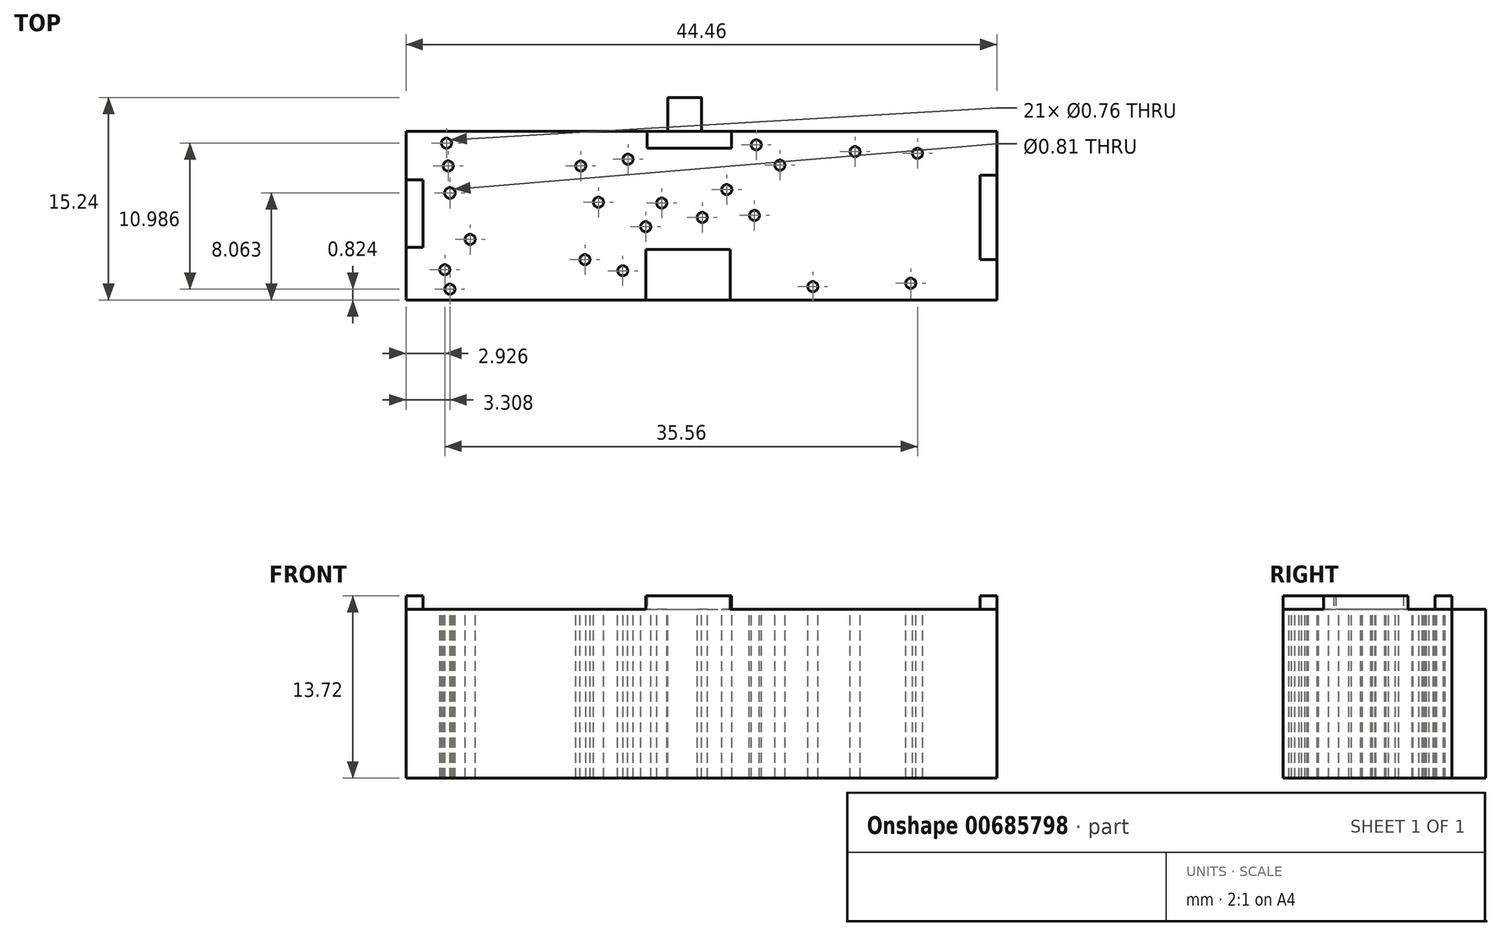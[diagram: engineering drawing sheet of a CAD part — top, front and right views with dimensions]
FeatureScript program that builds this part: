
annotation { "Feature Type Name" : "Feature", "Feature Type Description" : "" }
export const myFeature = defineFeature(function(context is Context, id is Id, definition is map)
    precondition{}
    {
        {
            var Q0;
            Q0=qCreatedBy(makeId("Top.planeOp"),FACE);
            var sketch = newSketch(context, id + "F0", { "sketchPlane" : qUnion([Q0])});
            skLineSegment(sketch, "E0", {"start": v(-5.35, -3.97) * mm, "end": v(-5.35, -4.1) * mm});
            skLineSegment(sketch, "E1", {"start": v(-5.35, -4.1) * mm, "end": v(-5.59, -4.44) * mm});
            skLineSegment(sketch, "E2", {"start": v(-5.59, -4.44) * mm, "end": v(-5.63, -4.47) * mm});
            skLineSegment(sketch, "E3", {"start": v(-5.63, -4.47) * mm, "end": v(-5.68, -4.5) * mm});
            skLineSegment(sketch, "E4", {"start": v(-5.68, -4.5) * mm, "end": v(-6.16, -4.5) * mm});
            skLineSegment(sketch, "E5", {"start": v(-6.16, -4.5) * mm, "end": v(-6.2, -4.47) * mm});
            skLineSegment(sketch, "E6", {"start": v(-6.2, -4.47) * mm, "end": v(-6.25, -4.44) * mm});
            skLineSegment(sketch, "E7", {"start": v(-6.25, -4.44) * mm, "end": v(-6.49, -4.09) * mm});
            skLineSegment(sketch, "E8", {"start": v(-6.49, -4.09) * mm, "end": v(-6.49, -3.97) * mm});
            skLineSegment(sketch, "E9", {"start": v(-6.49, -3.97) * mm, "end": v(-6.49, -3.85) * mm});
            skLineSegment(sketch, "E10", {"start": v(-6.49, -3.85) * mm, "end": v(-6.25, -3.5) * mm});
            skLineSegment(sketch, "E11", {"start": v(-6.25, -3.5) * mm, "end": v(-6.2, -3.48) * mm});
            skLineSegment(sketch, "E12", {"start": v(-6.2, -3.48) * mm, "end": v(-6.16, -3.45) * mm});
            skLineSegment(sketch, "E13", {"start": v(-6.16, -3.45) * mm, "end": v(-5.68, -3.45) * mm});
            skLineSegment(sketch, "E14", {"start": v(-5.68, -3.45) * mm, "end": v(-5.63, -3.48) * mm});
            skLineSegment(sketch, "E15", {"start": v(-5.63, -3.48) * mm, "end": v(-5.59, -3.5) * mm});
            skLineSegment(sketch, "E16", {"start": v(-5.59, -3.5) * mm, "end": v(-5.35, -3.85) * mm});
            skLineSegment(sketch, "E17", {"start": v(-5.35, -3.85) * mm, "end": v(-5.35, -3.97) * mm});
            skLineSegment(sketch, "E18", {"start": v(-18.73, -3.9) * mm, "end": v(-18.73, -4.02) * mm});
            skLineSegment(sketch, "E19", {"start": v(-18.73, -4.02) * mm, "end": v(-18.97, -4.36) * mm});
            skLineSegment(sketch, "E20", {"start": v(-18.97, -4.36) * mm, "end": v(-19.02, -4.39) * mm});
            skLineSegment(sketch, "E21", {"start": v(-19.02, -4.39) * mm, "end": v(-19.06, -4.41) * mm});
            skLineSegment(sketch, "E22", {"start": v(-19.06, -4.41) * mm, "end": v(-19.54, -4.41) * mm});
            skLineSegment(sketch, "E23", {"start": v(-19.54, -4.41) * mm, "end": v(-19.59, -4.39) * mm});
            skLineSegment(sketch, "E24", {"start": v(-19.59, -4.39) * mm, "end": v(-19.63, -4.36) * mm});
            skLineSegment(sketch, "E25", {"start": v(-19.63, -4.36) * mm, "end": v(-19.88, -4.01) * mm});
            skLineSegment(sketch, "E26", {"start": v(-19.88, -4.01) * mm, "end": v(-19.88, -3.9) * mm});
            skLineSegment(sketch, "E27", {"start": v(-19.88, -3.9) * mm, "end": v(-19.88, -3.77) * mm});
            skLineSegment(sketch, "E28", {"start": v(-19.88, -3.77) * mm, "end": v(-19.63, -3.43) * mm});
            skLineSegment(sketch, "E29", {"start": v(-19.63, -3.43) * mm, "end": v(-19.59, -3.4) * mm});
            skLineSegment(sketch, "E30", {"start": v(-19.59, -3.4) * mm, "end": v(-19.54, -3.37) * mm});
            skLineSegment(sketch, "E31", {"start": v(-19.54, -3.37) * mm, "end": v(-19.06, -3.37) * mm});
            skLineSegment(sketch, "E32", {"start": v(-19.06, -3.37) * mm, "end": v(-19.02, -3.4) * mm});
            skLineSegment(sketch, "E33", {"start": v(-19.02, -3.4) * mm, "end": v(-18.97, -3.43) * mm});
            skLineSegment(sketch, "E34", {"start": v(-18.97, -3.43) * mm, "end": v(-18.73, -3.78) * mm});
            skLineSegment(sketch, "E35", {"start": v(-18.73, -3.78) * mm, "end": v(-18.73, -3.9) * mm});
            skLineSegment(sketch, "E36", {"start": v(-18.35, -5.36) * mm, "end": v(-18.35, -5.48) * mm});
            skLineSegment(sketch, "E37", {"start": v(-18.35, -5.48) * mm, "end": v(-18.6, -5.82) * mm});
            skLineSegment(sketch, "E38", {"start": v(-18.6, -5.82) * mm, "end": v(-18.64, -5.85) * mm});
            skLineSegment(sketch, "E39", {"start": v(-18.64, -5.85) * mm, "end": v(-18.68, -5.88) * mm});
            skLineSegment(sketch, "E40", {"start": v(-18.68, -5.88) * mm, "end": v(-19.16, -5.88) * mm});
            skLineSegment(sketch, "E41", {"start": v(-19.16, -5.88) * mm, "end": v(-19.2, -5.85) * mm});
            skLineSegment(sketch, "E42", {"start": v(-19.2, -5.85) * mm, "end": v(-19.25, -5.82) * mm});
            skLineSegment(sketch, "E43", {"start": v(-19.25, -5.82) * mm, "end": v(-19.5, -5.47) * mm});
            skLineSegment(sketch, "E44", {"start": v(-19.5, -5.47) * mm, "end": v(-19.5, -5.36) * mm});
            skLineSegment(sketch, "E45", {"start": v(-19.5, -5.36) * mm, "end": v(-19.5, -5.23) * mm});
            skLineSegment(sketch, "E46", {"start": v(-19.5, -5.23) * mm, "end": v(-19.25, -4.89) * mm});
            skLineSegment(sketch, "E47", {"start": v(-19.25, -4.89) * mm, "end": v(-19.2, -4.86) * mm});
            skLineSegment(sketch, "E48", {"start": v(-19.2, -4.86) * mm, "end": v(-19.16, -4.83) * mm});
            skLineSegment(sketch, "E49", {"start": v(-19.16, -4.83) * mm, "end": v(-18.68, -4.83) * mm});
            skLineSegment(sketch, "E50", {"start": v(-18.68, -4.83) * mm, "end": v(-18.64, -4.86) * mm});
            skLineSegment(sketch, "E51", {"start": v(-18.64, -4.86) * mm, "end": v(-18.6, -4.89) * mm});
            skLineSegment(sketch, "E52", {"start": v(-18.6, -4.89) * mm, "end": v(-18.35, -5.24) * mm});
            skLineSegment(sketch, "E53", {"start": v(-18.35, -5.24) * mm, "end": v(-18.35, -5.36) * mm});
            skLineSegment(sketch, "E54", {"start": v(8.95, -5.17) * mm, "end": v(8.95, -5.29) * mm});
            skLineSegment(sketch, "E55", {"start": v(8.95, -5.29) * mm, "end": v(8.71, -5.63) * mm});
            skLineSegment(sketch, "E56", {"start": v(8.71, -5.63) * mm, "end": v(8.67, -5.66) * mm});
            skLineSegment(sketch, "E57", {"start": v(8.67, -5.66) * mm, "end": v(8.62, -5.69) * mm});
            skLineSegment(sketch, "E58", {"start": v(8.62, -5.69) * mm, "end": v(8.14, -5.69) * mm});
            skLineSegment(sketch, "E59", {"start": v(8.14, -5.69) * mm, "end": v(8.1, -5.66) * mm});
            skLineSegment(sketch, "E60", {"start": v(8.1, -5.66) * mm, "end": v(8.05, -5.63) * mm});
            skLineSegment(sketch, "E61", {"start": v(8.05, -5.63) * mm, "end": v(7.81, -5.28) * mm});
            skLineSegment(sketch, "E62", {"start": v(7.81, -5.28) * mm, "end": v(7.81, -5.17) * mm});
            skLineSegment(sketch, "E63", {"start": v(7.81, -5.17) * mm, "end": v(7.81, -5.04) * mm});
            skLineSegment(sketch, "E64", {"start": v(7.81, -5.04) * mm, "end": v(8.05, -4.7) * mm});
            skLineSegment(sketch, "E65", {"start": v(8.05, -4.7) * mm, "end": v(8.1, -4.67) * mm});
            skLineSegment(sketch, "E66", {"start": v(8.1, -4.67) * mm, "end": v(8.14, -4.64) * mm});
            skLineSegment(sketch, "E67", {"start": v(8.14, -4.64) * mm, "end": v(8.62, -4.64) * mm});
            skLineSegment(sketch, "E68", {"start": v(8.62, -4.64) * mm, "end": v(8.67, -4.67) * mm});
            skLineSegment(sketch, "E69", {"start": v(8.67, -4.67) * mm, "end": v(8.71, -4.7) * mm});
            skLineSegment(sketch, "E70", {"start": v(8.71, -4.7) * mm, "end": v(8.95, -5.05) * mm});
            skLineSegment(sketch, "E71", {"start": v(8.95, -5.05) * mm, "end": v(8.95, -5.17) * mm});
            skLineSegment(sketch, "E72", {"start": v(4.56, 0.2) * mm, "end": v(4.56, 0.07) * mm});
            skLineSegment(sketch, "E73", {"start": v(4.56, 0.07) * mm, "end": v(4.32, -0.27) * mm});
            skLineSegment(sketch, "E74", {"start": v(4.32, -0.27) * mm, "end": v(4.27, -0.3) * mm});
            skLineSegment(sketch, "E75", {"start": v(4.27, -0.3) * mm, "end": v(4.23, -0.33) * mm});
            skLineSegment(sketch, "E76", {"start": v(4.23, -0.33) * mm, "end": v(3.75, -0.33) * mm});
            skLineSegment(sketch, "E77", {"start": v(3.75, -0.33) * mm, "end": v(3.7, -0.3) * mm});
            skLineSegment(sketch, "E78", {"start": v(3.7, -0.3) * mm, "end": v(3.66, -0.27) * mm});
            skLineSegment(sketch, "E79", {"start": v(3.66, -0.27) * mm, "end": v(3.42, 0.08) * mm});
            skLineSegment(sketch, "E80", {"start": v(3.42, 0.08) * mm, "end": v(3.42, 0.2) * mm});
            skLineSegment(sketch, "E81", {"start": v(3.42, 0.2) * mm, "end": v(3.42, 0.32) * mm});
            skLineSegment(sketch, "E82", {"start": v(3.42, 0.32) * mm, "end": v(3.66, 0.66) * mm});
            skLineSegment(sketch, "E83", {"start": v(3.66, 0.66) * mm, "end": v(3.7, 0.69) * mm});
            skLineSegment(sketch, "E84", {"start": v(3.7, 0.69) * mm, "end": v(3.75, 0.71) * mm});
            skLineSegment(sketch, "E85", {"start": v(3.75, 0.71) * mm, "end": v(4.23, 0.71) * mm});
            skLineSegment(sketch, "E86", {"start": v(4.23, 0.71) * mm, "end": v(4.27, 0.69) * mm});
            skLineSegment(sketch, "E87", {"start": v(4.27, 0.69) * mm, "end": v(4.32, 0.66) * mm});
            skLineSegment(sketch, "E88", {"start": v(4.32, 0.66) * mm, "end": v(4.56, 0.31) * mm});
            skLineSegment(sketch, "E89", {"start": v(4.56, 0.31) * mm, "end": v(4.56, 0.2) * mm});
            skLineSegment(sketch, "E90", {"start": v(2.48, 2.14) * mm, "end": v(2.48, 2.01) * mm});
            skLineSegment(sketch, "E91", {"start": v(2.48, 2.01) * mm, "end": v(2.24, 1.67) * mm});
            skLineSegment(sketch, "E92", {"start": v(2.24, 1.67) * mm, "end": v(2.2, 1.64) * mm});
            skLineSegment(sketch, "E93", {"start": v(2.2, 1.64) * mm, "end": v(2.15, 1.62) * mm});
            skLineSegment(sketch, "E94", {"start": v(2.15, 1.62) * mm, "end": v(1.66, 1.62) * mm});
            skLineSegment(sketch, "E95", {"start": v(1.66, 1.62) * mm, "end": v(1.62, 1.64) * mm});
            skLineSegment(sketch, "E96", {"start": v(1.62, 1.64) * mm, "end": v(1.58, 1.67) * mm});
            skLineSegment(sketch, "E97", {"start": v(1.58, 1.67) * mm, "end": v(1.33, 2.02) * mm});
            skLineSegment(sketch, "E98", {"start": v(1.33, 2.02) * mm, "end": v(1.33, 2.14) * mm});
            skLineSegment(sketch, "E99", {"start": v(1.33, 2.14) * mm, "end": v(1.33, 2.26) * mm});
            skLineSegment(sketch, "E100", {"start": v(1.33, 2.26) * mm, "end": v(1.58, 2.6) * mm});
            skLineSegment(sketch, "E101", {"start": v(1.58, 2.6) * mm, "end": v(1.62, 2.63) * mm});
            skLineSegment(sketch, "E102", {"start": v(1.62, 2.63) * mm, "end": v(1.66, 2.66) * mm});
            skLineSegment(sketch, "E103", {"start": v(1.66, 2.66) * mm, "end": v(2.15, 2.66) * mm});
            skLineSegment(sketch, "E104", {"start": v(2.15, 2.66) * mm, "end": v(2.2, 2.63) * mm});
            skLineSegment(sketch, "E105", {"start": v(2.2, 2.63) * mm, "end": v(2.24, 2.6) * mm});
            skLineSegment(sketch, "E106", {"start": v(2.24, 2.6) * mm, "end": v(2.48, 2.26) * mm});
            skLineSegment(sketch, "E107", {"start": v(2.48, 2.26) * mm, "end": v(2.48, 2.14) * mm});
            skLineSegment(sketch, "E108", {"start": v(6.48, 3.98) * mm, "end": v(6.48, 3.86) * mm});
            skLineSegment(sketch, "E109", {"start": v(6.48, 3.86) * mm, "end": v(6.24, 3.5) * mm});
            skLineSegment(sketch, "E110", {"start": v(6.24, 3.5) * mm, "end": v(6.2, 3.48) * mm});
            skLineSegment(sketch, "E111", {"start": v(6.2, 3.48) * mm, "end": v(6.15, 3.46) * mm});
            skLineSegment(sketch, "E112", {"start": v(6.15, 3.46) * mm, "end": v(5.66, 3.46) * mm});
            skLineSegment(sketch, "E113", {"start": v(5.66, 3.46) * mm, "end": v(5.62, 3.48) * mm});
            skLineSegment(sketch, "E114", {"start": v(5.62, 3.48) * mm, "end": v(5.58, 3.5) * mm});
            skLineSegment(sketch, "E115", {"start": v(5.58, 3.5) * mm, "end": v(5.33, 3.86) * mm});
            skLineSegment(sketch, "E116", {"start": v(5.33, 3.86) * mm, "end": v(5.33, 3.98) * mm});
            skLineSegment(sketch, "E117", {"start": v(5.33, 3.98) * mm, "end": v(5.33, 4.1) * mm});
            skLineSegment(sketch, "E118", {"start": v(5.33, 4.1) * mm, "end": v(5.58, 4.45) * mm});
            skLineSegment(sketch, "E119", {"start": v(5.58, 4.45) * mm, "end": v(5.62, 4.47) * mm});
            skLineSegment(sketch, "E120", {"start": v(5.62, 4.47) * mm, "end": v(5.66, 4.5) * mm});
            skLineSegment(sketch, "E121", {"start": v(5.66, 4.5) * mm, "end": v(6.15, 4.5) * mm});
            skLineSegment(sketch, "E122", {"start": v(6.15, 4.5) * mm, "end": v(6.2, 4.47) * mm});
            skLineSegment(sketch, "E123", {"start": v(6.2, 4.47) * mm, "end": v(6.24, 4.45) * mm});
            skLineSegment(sketch, "E124", {"start": v(6.24, 4.45) * mm, "end": v(6.48, 4.1) * mm});
            skLineSegment(sketch, "E125", {"start": v(6.48, 4.1) * mm, "end": v(6.48, 3.98) * mm});
            skLineSegment(sketch, "E126", {"start": v(16.32, -4.91) * mm, "end": v(16.32, -5.03) * mm});
            skLineSegment(sketch, "E127", {"start": v(16.32, -5.03) * mm, "end": v(16.08, -5.38) * mm});
            skLineSegment(sketch, "E128", {"start": v(16.08, -5.38) * mm, "end": v(16.03, -5.4) * mm});
            skLineSegment(sketch, "E129", {"start": v(16.03, -5.4) * mm, "end": v(15.99, -5.43) * mm});
            skLineSegment(sketch, "E130", {"start": v(15.99, -5.43) * mm, "end": v(15.5, -5.43) * mm});
            skLineSegment(sketch, "E131", {"start": v(15.5, -5.43) * mm, "end": v(15.46, -5.4) * mm});
            skLineSegment(sketch, "E132", {"start": v(15.46, -5.4) * mm, "end": v(15.42, -5.38) * mm});
            skLineSegment(sketch, "E133", {"start": v(15.42, -5.38) * mm, "end": v(15.18, -5.03) * mm});
            skLineSegment(sketch, "E134", {"start": v(15.18, -5.03) * mm, "end": v(15.18, -4.91) * mm});
            skLineSegment(sketch, "E135", {"start": v(15.18, -4.91) * mm, "end": v(15.18, -4.79) * mm});
            skLineSegment(sketch, "E136", {"start": v(15.18, -4.79) * mm, "end": v(15.42, -4.44) * mm});
            skLineSegment(sketch, "E137", {"start": v(15.42, -4.44) * mm, "end": v(15.46, -4.42) * mm});
            skLineSegment(sketch, "E138", {"start": v(15.46, -4.42) * mm, "end": v(15.5, -4.39) * mm});
            skLineSegment(sketch, "E139", {"start": v(15.5, -4.39) * mm, "end": v(15.99, -4.39) * mm});
            skLineSegment(sketch, "E140", {"start": v(15.99, -4.39) * mm, "end": v(16.03, -4.42) * mm});
            skLineSegment(sketch, "E141", {"start": v(16.03, -4.42) * mm, "end": v(16.08, -4.44) * mm});
            skLineSegment(sketch, "E142", {"start": v(16.08, -4.44) * mm, "end": v(16.32, -4.8) * mm});
            skLineSegment(sketch, "E143", {"start": v(16.32, -4.8) * mm, "end": v(16.32, -4.91) * mm});
            skLineSegment(sketch, "E144", {"start": v(12.13, 5) * mm, "end": v(12.13, 4.87) * mm});
            skLineSegment(sketch, "E145", {"start": v(12.13, 4.87) * mm, "end": v(11.89, 4.53) * mm});
            skLineSegment(sketch, "E146", {"start": v(11.89, 4.53) * mm, "end": v(11.84, 4.5) * mm});
            skLineSegment(sketch, "E147", {"start": v(11.84, 4.5) * mm, "end": v(11.8, 4.48) * mm});
            skLineSegment(sketch, "E148", {"start": v(11.8, 4.48) * mm, "end": v(11.32, 4.48) * mm});
            skLineSegment(sketch, "E149", {"start": v(11.32, 4.48) * mm, "end": v(11.27, 4.5) * mm});
            skLineSegment(sketch, "E150", {"start": v(11.27, 4.5) * mm, "end": v(11.23, 4.53) * mm});
            skLineSegment(sketch, "E151", {"start": v(11.23, 4.53) * mm, "end": v(10.99, 4.88) * mm});
            skLineSegment(sketch, "E152", {"start": v(10.99, 4.88) * mm, "end": v(10.99, 5) * mm});
            skLineSegment(sketch, "E153", {"start": v(10.99, 5) * mm, "end": v(10.99, 5.12) * mm});
            skLineSegment(sketch, "E154", {"start": v(10.99, 5.12) * mm, "end": v(11.23, 5.46) * mm});
            skLineSegment(sketch, "E155", {"start": v(11.23, 5.46) * mm, "end": v(11.27, 5.49) * mm});
            skLineSegment(sketch, "E156", {"start": v(11.27, 5.49) * mm, "end": v(11.32, 5.52) * mm});
            skLineSegment(sketch, "E157", {"start": v(11.32, 5.52) * mm, "end": v(11.8, 5.52) * mm});
            skLineSegment(sketch, "E158", {"start": v(11.8, 5.52) * mm, "end": v(11.84, 5.49) * mm});
            skLineSegment(sketch, "E159", {"start": v(11.84, 5.49) * mm, "end": v(11.89, 5.46) * mm});
            skLineSegment(sketch, "E160", {"start": v(11.89, 5.46) * mm, "end": v(12.13, 5.11) * mm});
            skLineSegment(sketch, "E161", {"start": v(12.13, 5.11) * mm, "end": v(12.13, 5) * mm});
            skLineSegment(sketch, "E162", {"start": v(4.7, 5.5) * mm, "end": v(4.7, 5.38) * mm});
            skLineSegment(sketch, "E163", {"start": v(4.7, 5.38) * mm, "end": v(4.46, 5.03) * mm});
            skLineSegment(sketch, "E164", {"start": v(4.46, 5.03) * mm, "end": v(4.41, 5) * mm});
            skLineSegment(sketch, "E165", {"start": v(4.41, 5) * mm, "end": v(4.37, 4.98) * mm});
            skLineSegment(sketch, "E166", {"start": v(4.37, 4.98) * mm, "end": v(3.89, 4.98) * mm});
            skLineSegment(sketch, "E167", {"start": v(3.89, 4.98) * mm, "end": v(3.84, 5) * mm});
            skLineSegment(sketch, "E168", {"start": v(3.84, 5) * mm, "end": v(3.8, 5.03) * mm});
            skLineSegment(sketch, "E169", {"start": v(3.8, 5.03) * mm, "end": v(3.56, 5.39) * mm});
            skLineSegment(sketch, "E170", {"start": v(3.56, 5.39) * mm, "end": v(3.56, 5.5) * mm});
            skLineSegment(sketch, "E171", {"start": v(3.56, 5.5) * mm, "end": v(3.56, 5.63) * mm});
            skLineSegment(sketch, "E172", {"start": v(3.56, 5.63) * mm, "end": v(3.8, 5.97) * mm});
            skLineSegment(sketch, "E173", {"start": v(3.8, 5.97) * mm, "end": v(3.84, 6) * mm});
            skLineSegment(sketch, "E174", {"start": v(3.84, 6) * mm, "end": v(3.89, 6.02) * mm});
            skLineSegment(sketch, "E175", {"start": v(3.89, 6.02) * mm, "end": v(4.37, 6.02) * mm});
            skLineSegment(sketch, "E176", {"start": v(4.37, 6.02) * mm, "end": v(4.41, 6) * mm});
            skLineSegment(sketch, "E177", {"start": v(4.41, 6) * mm, "end": v(4.46, 5.97) * mm});
            skLineSegment(sketch, "E178", {"start": v(4.46, 5.97) * mm, "end": v(4.7, 5.62) * mm});
            skLineSegment(sketch, "E179", {"start": v(4.7, 5.62) * mm, "end": v(4.7, 5.5) * mm});
            skLineSegment(sketch, "E180", {"start": v(0.64, 0.04) * mm, "end": v(0.64, -0.08) * mm});
            skLineSegment(sketch, "E181", {"start": v(0.64, -0.08) * mm, "end": v(0.4, -0.43) * mm});
            skLineSegment(sketch, "E182", {"start": v(0.4, -0.43) * mm, "end": v(0.35, -0.45) * mm});
            skLineSegment(sketch, "E183", {"start": v(0.35, -0.45) * mm, "end": v(0.3, -0.48) * mm});
            skLineSegment(sketch, "E184", {"start": v(0.3, -0.48) * mm, "end": v(-0.18, -0.48) * mm});
            skLineSegment(sketch, "E185", {"start": v(-0.18, -0.48) * mm, "end": v(-0.22, -0.45) * mm});
            skLineSegment(sketch, "E186", {"start": v(-0.22, -0.45) * mm, "end": v(-0.27, -0.43) * mm});
            skLineSegment(sketch, "E187", {"start": v(-0.27, -0.43) * mm, "end": v(-0.5, -0.08) * mm});
            skLineSegment(sketch, "E188", {"start": v(-0.5, -0.08) * mm, "end": v(-0.5, 0.04) * mm});
            skLineSegment(sketch, "E189", {"start": v(-0.5, 0.04) * mm, "end": v(-0.5, 0.17) * mm});
            skLineSegment(sketch, "E190", {"start": v(-0.5, 0.17) * mm, "end": v(-0.27, 0.51) * mm});
            skLineSegment(sketch, "E191", {"start": v(-0.27, 0.51) * mm, "end": v(-0.22, 0.54) * mm});
            skLineSegment(sketch, "E192", {"start": v(-0.22, 0.54) * mm, "end": v(-0.18, 0.56) * mm});
            skLineSegment(sketch, "E193", {"start": v(-0.18, 0.56) * mm, "end": v(0.3, 0.56) * mm});
            skLineSegment(sketch, "E194", {"start": v(0.3, 0.56) * mm, "end": v(0.35, 0.54) * mm});
            skLineSegment(sketch, "E195", {"start": v(0.35, 0.54) * mm, "end": v(0.4, 0.51) * mm});
            skLineSegment(sketch, "E196", {"start": v(0.4, 0.51) * mm, "end": v(0.64, 0.16) * mm});
            skLineSegment(sketch, "E197", {"start": v(0.64, 0.16) * mm, "end": v(0.64, 0.04) * mm});
            skLineSegment(sketch, "E198", {"start": v(-16.83, -1.6) * mm, "end": v(-16.83, -1.73) * mm});
            skLineSegment(sketch, "E199", {"start": v(-16.83, -1.73) * mm, "end": v(-17.07, -2.08) * mm});
            skLineSegment(sketch, "E200", {"start": v(-17.07, -2.08) * mm, "end": v(-17.11, -2.1) * mm});
            skLineSegment(sketch, "E201", {"start": v(-17.11, -2.1) * mm, "end": v(-17.16, -2.13) * mm});
            skLineSegment(sketch, "E202", {"start": v(-17.16, -2.13) * mm, "end": v(-17.64, -2.13) * mm});
            skLineSegment(sketch, "E203", {"start": v(-17.64, -2.13) * mm, "end": v(-17.68, -2.1) * mm});
            skLineSegment(sketch, "E204", {"start": v(-17.68, -2.1) * mm, "end": v(-17.73, -2.08) * mm});
            skLineSegment(sketch, "E205", {"start": v(-17.73, -2.08) * mm, "end": v(-17.97, -1.73) * mm});
            skLineSegment(sketch, "E206", {"start": v(-17.97, -1.73) * mm, "end": v(-17.97, -1.6) * mm});
            skLineSegment(sketch, "E207", {"start": v(-17.97, -1.6) * mm, "end": v(-17.97, -1.48) * mm});
            skLineSegment(sketch, "E208", {"start": v(-17.97, -1.48) * mm, "end": v(-17.73, -1.14) * mm});
            skLineSegment(sketch, "E209", {"start": v(-17.73, -1.14) * mm, "end": v(-17.68, -1.11) * mm});
            skLineSegment(sketch, "E210", {"start": v(-17.68, -1.11) * mm, "end": v(-17.64, -1.09) * mm});
            skLineSegment(sketch, "E211", {"start": v(-17.64, -1.09) * mm, "end": v(-17.16, -1.09) * mm});
            skLineSegment(sketch, "E212", {"start": v(-17.16, -1.09) * mm, "end": v(-17.11, -1.11) * mm});
            skLineSegment(sketch, "E213", {"start": v(-17.11, -1.11) * mm, "end": v(-17.07, -1.14) * mm});
            skLineSegment(sketch, "E214", {"start": v(-17.07, -1.14) * mm, "end": v(-16.83, -1.5) * mm});
            skLineSegment(sketch, "E215", {"start": v(-16.83, -1.5) * mm, "end": v(-16.83, -1.6) * mm});
            skLineSegment(sketch, "E216", {"start": v(-8.2, -3.13) * mm, "end": v(-8.2, -3.26) * mm});
            skLineSegment(sketch, "E217", {"start": v(-8.2, -3.26) * mm, "end": v(-8.43, -3.6) * mm});
            skLineSegment(sketch, "E218", {"start": v(-8.43, -3.6) * mm, "end": v(-8.48, -3.63) * mm});
            skLineSegment(sketch, "E219", {"start": v(-8.48, -3.63) * mm, "end": v(-8.52, -3.65) * mm});
            skLineSegment(sketch, "E220", {"start": v(-8.52, -3.65) * mm, "end": v(-9, -3.65) * mm});
            skLineSegment(sketch, "E221", {"start": v(-9, -3.65) * mm, "end": v(-9.05, -3.63) * mm});
            skLineSegment(sketch, "E222", {"start": v(-9.05, -3.63) * mm, "end": v(-9.1, -3.6) * mm});
            skLineSegment(sketch, "E223", {"start": v(-9.1, -3.6) * mm, "end": v(-9.33, -3.25) * mm});
            skLineSegment(sketch, "E224", {"start": v(-9.33, -3.25) * mm, "end": v(-9.33, -3.13) * mm});
            skLineSegment(sketch, "E225", {"start": v(-9.33, -3.13) * mm, "end": v(-9.33, -3) * mm});
            skLineSegment(sketch, "E226", {"start": v(-9.33, -3) * mm, "end": v(-9.1, -2.66) * mm});
            skLineSegment(sketch, "E227", {"start": v(-9.1, -2.66) * mm, "end": v(-9.05, -2.64) * mm});
            skLineSegment(sketch, "E228", {"start": v(-9.05, -2.64) * mm, "end": v(-9, -2.61) * mm});
            skLineSegment(sketch, "E229", {"start": v(-9, -2.61) * mm, "end": v(-8.52, -2.61) * mm});
            skLineSegment(sketch, "E230", {"start": v(-8.52, -2.61) * mm, "end": v(-8.48, -2.64) * mm});
            skLineSegment(sketch, "E231", {"start": v(-8.48, -2.64) * mm, "end": v(-8.43, -2.66) * mm});
            skLineSegment(sketch, "E232", {"start": v(-8.43, -2.66) * mm, "end": v(-8.2, -3.01) * mm});
            skLineSegment(sketch, "E233", {"start": v(-8.2, -3.01) * mm, "end": v(-8.2, -3.13) * mm});
            skLineSegment(sketch, "E234", {"start": v(-3.62, -0.66) * mm, "end": v(-3.62, -0.78) * mm});
            skLineSegment(sketch, "E235", {"start": v(-3.62, -0.78) * mm, "end": v(-3.86, -1.13) * mm});
            skLineSegment(sketch, "E236", {"start": v(-3.86, -1.13) * mm, "end": v(-3.9, -1.15) * mm});
            skLineSegment(sketch, "E237", {"start": v(-3.9, -1.15) * mm, "end": v(-3.95, -1.18) * mm});
            skLineSegment(sketch, "E238", {"start": v(-3.95, -1.18) * mm, "end": v(-4.43, -1.18) * mm});
            skLineSegment(sketch, "E239", {"start": v(-4.43, -1.18) * mm, "end": v(-4.48, -1.15) * mm});
            skLineSegment(sketch, "E240", {"start": v(-4.48, -1.15) * mm, "end": v(-4.52, -1.13) * mm});
            skLineSegment(sketch, "E241", {"start": v(-4.52, -1.13) * mm, "end": v(-4.76, -0.77) * mm});
            skLineSegment(sketch, "E242", {"start": v(-4.76, -0.77) * mm, "end": v(-4.76, -0.66) * mm});
            skLineSegment(sketch, "E243", {"start": v(-4.76, -0.66) * mm, "end": v(-4.76, -0.53) * mm});
            skLineSegment(sketch, "E244", {"start": v(-4.76, -0.53) * mm, "end": v(-4.52, -0.19) * mm});
            skLineSegment(sketch, "E245", {"start": v(-4.52, -0.19) * mm, "end": v(-4.48, -0.16) * mm});
            skLineSegment(sketch, "E246", {"start": v(-4.48, -0.16) * mm, "end": v(-4.43, -0.14) * mm});
            skLineSegment(sketch, "E247", {"start": v(-4.43, -0.14) * mm, "end": v(-3.95, -0.14) * mm});
            skLineSegment(sketch, "E248", {"start": v(-3.95, -0.14) * mm, "end": v(-3.9, -0.16) * mm});
            skLineSegment(sketch, "E249", {"start": v(-3.9, -0.16) * mm, "end": v(-3.86, -0.19) * mm});
            skLineSegment(sketch, "E250", {"start": v(-3.86, -0.19) * mm, "end": v(-3.62, -0.54) * mm});
            skLineSegment(sketch, "E251", {"start": v(-3.62, -0.54) * mm, "end": v(-3.62, -0.66) * mm});
            skLineSegment(sketch, "E252", {"start": v(-7.18, 1.18) * mm, "end": v(-7.18, 1.06) * mm});
            skLineSegment(sketch, "E253", {"start": v(-7.18, 1.06) * mm, "end": v(-7.42, 0.72) * mm});
            skLineSegment(sketch, "E254", {"start": v(-7.42, 0.72) * mm, "end": v(-7.46, 0.69) * mm});
            skLineSegment(sketch, "E255", {"start": v(-7.46, 0.69) * mm, "end": v(-7.5, 0.66) * mm});
            skLineSegment(sketch, "E256", {"start": v(-7.5, 0.66) * mm, "end": v(-7.99, 0.66) * mm});
            skLineSegment(sketch, "E257", {"start": v(-7.99, 0.66) * mm, "end": v(-8.03, 0.69) * mm});
            skLineSegment(sketch, "E258", {"start": v(-8.03, 0.69) * mm, "end": v(-8.08, 0.72) * mm});
            skLineSegment(sketch, "E259", {"start": v(-8.08, 0.72) * mm, "end": v(-8.32, 1.07) * mm});
            skLineSegment(sketch, "E260", {"start": v(-8.32, 1.07) * mm, "end": v(-8.32, 1.18) * mm});
            skLineSegment(sketch, "E261", {"start": v(-8.32, 1.18) * mm, "end": v(-8.32, 1.3) * mm});
            skLineSegment(sketch, "E262", {"start": v(-8.32, 1.3) * mm, "end": v(-8.08, 1.65) * mm});
            skLineSegment(sketch, "E263", {"start": v(-8.08, 1.65) * mm, "end": v(-8.03, 1.68) * mm});
            skLineSegment(sketch, "E264", {"start": v(-8.03, 1.68) * mm, "end": v(-7.99, 1.7) * mm});
            skLineSegment(sketch, "E265", {"start": v(-7.99, 1.7) * mm, "end": v(-7.5, 1.7) * mm});
            skLineSegment(sketch, "E266", {"start": v(-7.5, 1.7) * mm, "end": v(-7.46, 1.68) * mm});
            skLineSegment(sketch, "E267", {"start": v(-7.46, 1.68) * mm, "end": v(-7.42, 1.65) * mm});
            skLineSegment(sketch, "E268", {"start": v(-7.42, 1.65) * mm, "end": v(-7.18, 1.3) * mm});
            skLineSegment(sketch, "E269", {"start": v(-7.18, 1.3) * mm, "end": v(-7.18, 1.18) * mm});
            skLineSegment(sketch, "E270", {"start": v(-2.41, 1.12) * mm, "end": v(-2.41, 1) * mm});
            skLineSegment(sketch, "E271", {"start": v(-2.41, 1) * mm, "end": v(-2.65, 0.65) * mm});
            skLineSegment(sketch, "E272", {"start": v(-2.65, 0.65) * mm, "end": v(-2.7, 0.63) * mm});
            skLineSegment(sketch, "E273", {"start": v(-2.7, 0.63) * mm, "end": v(-2.74, 0.6) * mm});
            skLineSegment(sketch, "E274", {"start": v(-2.74, 0.6) * mm, "end": v(-3.23, 0.6) * mm});
            skLineSegment(sketch, "E275", {"start": v(-3.23, 0.6) * mm, "end": v(-3.27, 0.63) * mm});
            skLineSegment(sketch, "E276", {"start": v(-3.27, 0.63) * mm, "end": v(-3.31, 0.65) * mm});
            skLineSegment(sketch, "E277", {"start": v(-3.31, 0.65) * mm, "end": v(-3.56, 1) * mm});
            skLineSegment(sketch, "E278", {"start": v(-3.56, 1) * mm, "end": v(-3.56, 1.12) * mm});
            skLineSegment(sketch, "E279", {"start": v(-3.56, 1.12) * mm, "end": v(-3.56, 1.25) * mm});
            skLineSegment(sketch, "E280", {"start": v(-3.56, 1.25) * mm, "end": v(-3.31, 1.6) * mm});
            skLineSegment(sketch, "E281", {"start": v(-3.31, 1.6) * mm, "end": v(-3.27, 1.62) * mm});
            skLineSegment(sketch, "E282", {"start": v(-3.27, 1.62) * mm, "end": v(-3.23, 1.64) * mm});
            skLineSegment(sketch, "E283", {"start": v(-3.23, 1.64) * mm, "end": v(-2.74, 1.64) * mm});
            skLineSegment(sketch, "E284", {"start": v(-2.74, 1.64) * mm, "end": v(-2.7, 1.62) * mm});
            skLineSegment(sketch, "E285", {"start": v(-2.7, 1.62) * mm, "end": v(-2.65, 1.6) * mm});
            skLineSegment(sketch, "E286", {"start": v(-2.65, 1.6) * mm, "end": v(-2.41, 1.24) * mm});
            skLineSegment(sketch, "E287", {"start": v(-2.41, 1.24) * mm, "end": v(-2.41, 1.12) * mm});
            skLineSegment(sketch, "E288", {"start": v(16.83, 4.87) * mm, "end": v(16.83, 4.75) * mm});
            skLineSegment(sketch, "E289", {"start": v(16.83, 4.75) * mm, "end": v(16.59, 4.4) * mm});
            skLineSegment(sketch, "E290", {"start": v(16.59, 4.4) * mm, "end": v(16.54, 4.37) * mm});
            skLineSegment(sketch, "E291", {"start": v(16.54, 4.37) * mm, "end": v(16.5, 4.35) * mm});
            skLineSegment(sketch, "E292", {"start": v(16.5, 4.35) * mm, "end": v(16.01, 4.35) * mm});
            skLineSegment(sketch, "E293", {"start": v(16.01, 4.35) * mm, "end": v(15.97, 4.37) * mm});
            skLineSegment(sketch, "E294", {"start": v(15.97, 4.37) * mm, "end": v(15.93, 4.4) * mm});
            skLineSegment(sketch, "E295", {"start": v(15.93, 4.4) * mm, "end": v(15.68, 4.75) * mm});
            skLineSegment(sketch, "E296", {"start": v(15.68, 4.75) * mm, "end": v(15.68, 4.87) * mm});
            skLineSegment(sketch, "E297", {"start": v(15.68, 4.87) * mm, "end": v(15.68, 5) * mm});
            skLineSegment(sketch, "E298", {"start": v(15.68, 5) * mm, "end": v(15.93, 5.34) * mm});
            skLineSegment(sketch, "E299", {"start": v(15.93, 5.34) * mm, "end": v(15.97, 5.36) * mm});
            skLineSegment(sketch, "E300", {"start": v(15.97, 5.36) * mm, "end": v(16.01, 5.39) * mm});
            skLineSegment(sketch, "E301", {"start": v(16.01, 5.39) * mm, "end": v(16.5, 5.39) * mm});
            skLineSegment(sketch, "E302", {"start": v(16.5, 5.39) * mm, "end": v(16.54, 5.36) * mm});
            skLineSegment(sketch, "E303", {"start": v(16.54, 5.36) * mm, "end": v(16.59, 5.34) * mm});
            skLineSegment(sketch, "E304", {"start": v(16.59, 5.34) * mm, "end": v(16.83, 4.99) * mm});
            skLineSegment(sketch, "E305", {"start": v(16.83, 4.99) * mm, "end": v(16.83, 4.87) * mm});
            skLineSegment(sketch, "E306", {"start": v(-4.95, 4.42) * mm, "end": v(-4.95, 4.3) * mm});
            skLineSegment(sketch, "E307", {"start": v(-4.95, 4.3) * mm, "end": v(-5.2, 3.95) * mm});
            skLineSegment(sketch, "E308", {"start": v(-5.2, 3.95) * mm, "end": v(-5.24, 3.93) * mm});
            skLineSegment(sketch, "E309", {"start": v(-5.24, 3.93) * mm, "end": v(-5.28, 3.9) * mm});
            skLineSegment(sketch, "E310", {"start": v(-5.28, 3.9) * mm, "end": v(-5.77, 3.9) * mm});
            skLineSegment(sketch, "E311", {"start": v(-5.77, 3.9) * mm, "end": v(-5.8, 3.93) * mm});
            skLineSegment(sketch, "E312", {"start": v(-5.8, 3.93) * mm, "end": v(-5.85, 3.95) * mm});
            skLineSegment(sketch, "E313", {"start": v(-5.85, 3.95) * mm, "end": v(-6.1, 4.3) * mm});
            skLineSegment(sketch, "E314", {"start": v(-6.1, 4.3) * mm, "end": v(-6.1, 4.42) * mm});
            skLineSegment(sketch, "E315", {"start": v(-6.1, 4.42) * mm, "end": v(-6.1, 4.55) * mm});
            skLineSegment(sketch, "E316", {"start": v(-6.1, 4.55) * mm, "end": v(-5.85, 4.9) * mm});
            skLineSegment(sketch, "E317", {"start": v(-5.85, 4.9) * mm, "end": v(-5.8, 4.92) * mm});
            skLineSegment(sketch, "E318", {"start": v(-5.8, 4.92) * mm, "end": v(-5.77, 4.94) * mm});
            skLineSegment(sketch, "E319", {"start": v(-5.77, 4.94) * mm, "end": v(-5.28, 4.94) * mm});
            skLineSegment(sketch, "E320", {"start": v(-5.28, 4.94) * mm, "end": v(-5.24, 4.92) * mm});
            skLineSegment(sketch, "E321", {"start": v(-5.24, 4.92) * mm, "end": v(-5.2, 4.9) * mm});
            skLineSegment(sketch, "E322", {"start": v(-5.2, 4.9) * mm, "end": v(-4.95, 4.54) * mm});
            skLineSegment(sketch, "E323", {"start": v(-4.95, 4.54) * mm, "end": v(-4.95, 4.42) * mm});
            skLineSegment(sketch, "E324", {"start": v(-8.5, 3.92) * mm, "end": v(-8.5, 3.8) * mm});
            skLineSegment(sketch, "E325", {"start": v(-8.5, 3.8) * mm, "end": v(-8.75, 3.45) * mm});
            skLineSegment(sketch, "E326", {"start": v(-8.75, 3.45) * mm, "end": v(-8.8, 3.42) * mm});
            skLineSegment(sketch, "E327", {"start": v(-8.8, 3.42) * mm, "end": v(-8.84, 3.4) * mm});
            skLineSegment(sketch, "E328", {"start": v(-8.84, 3.4) * mm, "end": v(-9.32, 3.4) * mm});
            skLineSegment(sketch, "E329", {"start": v(-9.32, 3.4) * mm, "end": v(-9.37, 3.42) * mm});
            skLineSegment(sketch, "E330", {"start": v(-9.37, 3.42) * mm, "end": v(-9.41, 3.45) * mm});
            skLineSegment(sketch, "E331", {"start": v(-9.41, 3.45) * mm, "end": v(-9.65, 3.8) * mm});
            skLineSegment(sketch, "E332", {"start": v(-9.65, 3.8) * mm, "end": v(-9.65, 3.92) * mm});
            skLineSegment(sketch, "E333", {"start": v(-9.65, 3.92) * mm, "end": v(-9.65, 4.04) * mm});
            skLineSegment(sketch, "E334", {"start": v(-9.65, 4.04) * mm, "end": v(-9.41, 4.39) * mm});
            skLineSegment(sketch, "E335", {"start": v(-9.41, 4.39) * mm, "end": v(-9.37, 4.41) * mm});
            skLineSegment(sketch, "E336", {"start": v(-9.37, 4.41) * mm, "end": v(-9.32, 4.44) * mm});
            skLineSegment(sketch, "E337", {"start": v(-9.32, 4.44) * mm, "end": v(-8.84, 4.44) * mm});
            skLineSegment(sketch, "E338", {"start": v(-8.84, 4.44) * mm, "end": v(-8.8, 4.41) * mm});
            skLineSegment(sketch, "E339", {"start": v(-8.8, 4.41) * mm, "end": v(-8.75, 4.39) * mm});
            skLineSegment(sketch, "E340", {"start": v(-8.75, 4.39) * mm, "end": v(-8.5, 4.03) * mm});
            skLineSegment(sketch, "E341", {"start": v(-8.5, 4.03) * mm, "end": v(-8.5, 3.92) * mm});
            skLineSegment(sketch, "E342", {"start": v(-18.48, 3.92) * mm, "end": v(-18.48, 3.8) * mm});
            skLineSegment(sketch, "E343", {"start": v(-18.48, 3.8) * mm, "end": v(-18.72, 3.45) * mm});
            skLineSegment(sketch, "E344", {"start": v(-18.72, 3.45) * mm, "end": v(-18.76, 3.42) * mm});
            skLineSegment(sketch, "E345", {"start": v(-18.76, 3.42) * mm, "end": v(-18.8, 3.4) * mm});
            skLineSegment(sketch, "E346", {"start": v(-18.8, 3.4) * mm, "end": v(-19.3, 3.4) * mm});
            skLineSegment(sketch, "E347", {"start": v(-19.3, 3.4) * mm, "end": v(-19.34, 3.42) * mm});
            skLineSegment(sketch, "E348", {"start": v(-19.34, 3.42) * mm, "end": v(-19.38, 3.45) * mm});
            skLineSegment(sketch, "E349", {"start": v(-19.38, 3.45) * mm, "end": v(-19.62, 3.8) * mm});
            skLineSegment(sketch, "E350", {"start": v(-19.62, 3.8) * mm, "end": v(-19.62, 3.92) * mm});
            skLineSegment(sketch, "E351", {"start": v(-19.62, 3.92) * mm, "end": v(-19.62, 4.04) * mm});
            skLineSegment(sketch, "E352", {"start": v(-19.62, 4.04) * mm, "end": v(-19.38, 4.39) * mm});
            skLineSegment(sketch, "E353", {"start": v(-19.38, 4.39) * mm, "end": v(-19.34, 4.41) * mm});
            skLineSegment(sketch, "E354", {"start": v(-19.34, 4.41) * mm, "end": v(-19.3, 4.44) * mm});
            skLineSegment(sketch, "E355", {"start": v(-19.3, 4.44) * mm, "end": v(-18.8, 4.44) * mm});
            skLineSegment(sketch, "E356", {"start": v(-18.8, 4.44) * mm, "end": v(-18.76, 4.41) * mm});
            skLineSegment(sketch, "E357", {"start": v(-18.76, 4.41) * mm, "end": v(-18.72, 4.39) * mm});
            skLineSegment(sketch, "E358", {"start": v(-18.72, 4.39) * mm, "end": v(-18.48, 4.03) * mm});
            skLineSegment(sketch, "E359", {"start": v(-18.48, 4.03) * mm, "end": v(-18.48, 3.92) * mm});
            skLineSegment(sketch, "E360", {"start": v(-18.35, 1.88) * mm, "end": v(-18.35, 1.76) * mm});
            skLineSegment(sketch, "E361", {"start": v(-18.35, 1.76) * mm, "end": v(-18.6, 1.41) * mm});
            skLineSegment(sketch, "E362", {"start": v(-18.6, 1.41) * mm, "end": v(-18.64, 1.39) * mm});
            skLineSegment(sketch, "E363", {"start": v(-18.64, 1.39) * mm, "end": v(-18.68, 1.36) * mm});
            skLineSegment(sketch, "E364", {"start": v(-18.68, 1.36) * mm, "end": v(-19.16, 1.36) * mm});
            skLineSegment(sketch, "E365", {"start": v(-19.16, 1.36) * mm, "end": v(-19.2, 1.39) * mm});
            skLineSegment(sketch, "E366", {"start": v(-19.2, 1.39) * mm, "end": v(-19.25, 1.41) * mm});
            skLineSegment(sketch, "E367", {"start": v(-19.25, 1.41) * mm, "end": v(-19.5, 1.77) * mm});
            skLineSegment(sketch, "E368", {"start": v(-19.5, 1.77) * mm, "end": v(-19.5, 1.88) * mm});
            skLineSegment(sketch, "E369", {"start": v(-19.5, 1.88) * mm, "end": v(-19.5, 2) * mm});
            skLineSegment(sketch, "E370", {"start": v(-19.5, 2) * mm, "end": v(-19.25, 2.35) * mm});
            skLineSegment(sketch, "E371", {"start": v(-19.25, 2.35) * mm, "end": v(-19.2, 2.38) * mm});
            skLineSegment(sketch, "E372", {"start": v(-19.2, 2.38) * mm, "end": v(-19.16, 2.4) * mm});
            skLineSegment(sketch, "E373", {"start": v(-19.16, 2.4) * mm, "end": v(-18.68, 2.4) * mm});
            skLineSegment(sketch, "E374", {"start": v(-18.68, 2.4) * mm, "end": v(-18.64, 2.38) * mm});
            skLineSegment(sketch, "E375", {"start": v(-18.64, 2.38) * mm, "end": v(-18.6, 2.35) * mm});
            skLineSegment(sketch, "E376", {"start": v(-18.6, 2.35) * mm, "end": v(-18.35, 2) * mm});
            skLineSegment(sketch, "E377", {"start": v(-18.35, 2) * mm, "end": v(-18.35, 1.88) * mm});
            skLineSegment(sketch, "E378", {"start": v(-18.6, 5.63) * mm, "end": v(-18.6, 5.5) * mm});
            skLineSegment(sketch, "E379", {"start": v(-18.6, 5.5) * mm, "end": v(-18.85, 5.16) * mm});
            skLineSegment(sketch, "E380", {"start": v(-18.85, 5.16) * mm, "end": v(-18.9, 5.14) * mm});
            skLineSegment(sketch, "E381", {"start": v(-18.9, 5.14) * mm, "end": v(-18.94, 5.11) * mm});
            skLineSegment(sketch, "E382", {"start": v(-18.94, 5.11) * mm, "end": v(-19.42, 5.11) * mm});
            skLineSegment(sketch, "E383", {"start": v(-19.42, 5.11) * mm, "end": v(-19.46, 5.14) * mm});
            skLineSegment(sketch, "E384", {"start": v(-19.46, 5.14) * mm, "end": v(-19.5, 5.16) * mm});
            skLineSegment(sketch, "E385", {"start": v(-19.5, 5.16) * mm, "end": v(-19.75, 5.51) * mm});
            skLineSegment(sketch, "E386", {"start": v(-19.75, 5.51) * mm, "end": v(-19.75, 5.63) * mm});
            skLineSegment(sketch, "E387", {"start": v(-19.75, 5.63) * mm, "end": v(-19.75, 5.75) * mm});
            skLineSegment(sketch, "E388", {"start": v(-19.75, 5.75) * mm, "end": v(-19.5, 6.1) * mm});
            skLineSegment(sketch, "E389", {"start": v(-19.5, 6.1) * mm, "end": v(-19.46, 6.12) * mm});
            skLineSegment(sketch, "E390", {"start": v(-19.46, 6.12) * mm, "end": v(-19.42, 6.15) * mm});
            skLineSegment(sketch, "E391", {"start": v(-19.42, 6.15) * mm, "end": v(-18.94, 6.15) * mm});
            skLineSegment(sketch, "E392", {"start": v(-18.94, 6.15) * mm, "end": v(-18.9, 6.12) * mm});
            skLineSegment(sketch, "E393", {"start": v(-18.9, 6.12) * mm, "end": v(-18.85, 6.1) * mm});
            skLineSegment(sketch, "E394", {"start": v(-18.85, 6.1) * mm, "end": v(-18.6, 5.75) * mm});
            skLineSegment(sketch, "E395", {"start": v(-18.6, 5.75) * mm, "end": v(-18.6, 5.63) * mm});
            skLineSegment(sketch, "E396", {"start": v(-5.54, -3.97) * mm, "end": v(-5.54, -4.05) * mm});
            skLineSegment(sketch, "E397", {"start": v(-5.54, -4.05) * mm, "end": v(-5.7, -4.28) * mm});
            skLineSegment(sketch, "E398", {"start": v(-5.7, -4.28) * mm, "end": v(-5.73, -4.3) * mm});
            skLineSegment(sketch, "E399", {"start": v(-5.73, -4.3) * mm, "end": v(-5.76, -4.32) * mm});
            skLineSegment(sketch, "E400", {"start": v(-5.76, -4.32) * mm, "end": v(-6.08, -4.32) * mm});
            skLineSegment(sketch, "E401", {"start": v(-6.08, -4.32) * mm, "end": v(-6.1, -4.3) * mm});
            skLineSegment(sketch, "E402", {"start": v(-6.1, -4.3) * mm, "end": v(-6.14, -4.28) * mm});
            skLineSegment(sketch, "E403", {"start": v(-6.14, -4.28) * mm, "end": v(-6.3, -4.05) * mm});
            skLineSegment(sketch, "E404", {"start": v(-6.3, -4.05) * mm, "end": v(-6.3, -3.97) * mm});
            skLineSegment(sketch, "E405", {"start": v(-6.3, -3.97) * mm, "end": v(-6.3, -3.89) * mm});
            skLineSegment(sketch, "E406", {"start": v(-6.3, -3.89) * mm, "end": v(-6.14, -3.66) * mm});
            skLineSegment(sketch, "E407", {"start": v(-6.14, -3.66) * mm, "end": v(-6.1, -3.64) * mm});
            skLineSegment(sketch, "E408", {"start": v(-6.1, -3.64) * mm, "end": v(-6.08, -3.62) * mm});
            skLineSegment(sketch, "E409", {"start": v(-6.08, -3.62) * mm, "end": v(-5.76, -3.62) * mm});
            skLineSegment(sketch, "E410", {"start": v(-5.76, -3.62) * mm, "end": v(-5.73, -3.64) * mm});
            skLineSegment(sketch, "E411", {"start": v(-5.73, -3.64) * mm, "end": v(-5.7, -3.66) * mm});
            skLineSegment(sketch, "E412", {"start": v(-5.7, -3.66) * mm, "end": v(-5.54, -3.9) * mm});
            skLineSegment(sketch, "E413", {"start": v(-5.54, -3.9) * mm, "end": v(-5.54, -3.97) * mm});
            skLineSegment(sketch, "E414", {"start": v(-18.92, -3.9) * mm, "end": v(-18.92, -3.98) * mm});
            skLineSegment(sketch, "E415", {"start": v(-18.92, -3.98) * mm, "end": v(-19.08, -4.2) * mm});
            skLineSegment(sketch, "E416", {"start": v(-19.08, -4.2) * mm, "end": v(-19.11, -4.23) * mm});
            skLineSegment(sketch, "E417", {"start": v(-19.11, -4.23) * mm, "end": v(-19.14, -4.24) * mm});
            skLineSegment(sketch, "E418", {"start": v(-19.14, -4.24) * mm, "end": v(-19.46, -4.24) * mm});
            skLineSegment(sketch, "E419", {"start": v(-19.46, -4.24) * mm, "end": v(-19.5, -4.23) * mm});
            skLineSegment(sketch, "E420", {"start": v(-19.5, -4.23) * mm, "end": v(-19.52, -4.2) * mm});
            skLineSegment(sketch, "E421", {"start": v(-19.52, -4.2) * mm, "end": v(-19.68, -3.97) * mm});
            skLineSegment(sketch, "E422", {"start": v(-19.68, -3.97) * mm, "end": v(-19.68, -3.9) * mm});
            skLineSegment(sketch, "E423", {"start": v(-19.68, -3.9) * mm, "end": v(-19.68, -3.81) * mm});
            skLineSegment(sketch, "E424", {"start": v(-19.68, -3.81) * mm, "end": v(-19.52, -3.58) * mm});
            skLineSegment(sketch, "E425", {"start": v(-19.52, -3.58) * mm, "end": v(-19.5, -3.57) * mm});
            skLineSegment(sketch, "E426", {"start": v(-19.5, -3.57) * mm, "end": v(-19.46, -3.55) * mm});
            skLineSegment(sketch, "E427", {"start": v(-19.46, -3.55) * mm, "end": v(-19.14, -3.55) * mm});
            skLineSegment(sketch, "E428", {"start": v(-19.14, -3.55) * mm, "end": v(-19.11, -3.57) * mm});
            skLineSegment(sketch, "E429", {"start": v(-19.11, -3.57) * mm, "end": v(-19.08, -3.58) * mm});
            skLineSegment(sketch, "E430", {"start": v(-19.08, -3.58) * mm, "end": v(-18.92, -3.82) * mm});
            skLineSegment(sketch, "E431", {"start": v(-18.92, -3.82) * mm, "end": v(-18.92, -3.9) * mm});
            skLineSegment(sketch, "E432", {"start": v(-18.54, -5.36) * mm, "end": v(-18.54, -5.44) * mm});
            skLineSegment(sketch, "E433", {"start": v(-18.54, -5.44) * mm, "end": v(-18.7, -5.67) * mm});
            skLineSegment(sketch, "E434", {"start": v(-18.7, -5.67) * mm, "end": v(-18.73, -5.69) * mm});
            skLineSegment(sketch, "E435", {"start": v(-18.73, -5.69) * mm, "end": v(-18.76, -5.7) * mm});
            skLineSegment(sketch, "E436", {"start": v(-18.76, -5.7) * mm, "end": v(-19.08, -5.7) * mm});
            skLineSegment(sketch, "E437", {"start": v(-19.08, -5.7) * mm, "end": v(-19.11, -5.69) * mm});
            skLineSegment(sketch, "E438", {"start": v(-19.11, -5.69) * mm, "end": v(-19.14, -5.67) * mm});
            skLineSegment(sketch, "E439", {"start": v(-19.14, -5.67) * mm, "end": v(-19.3, -5.43) * mm});
            skLineSegment(sketch, "E440", {"start": v(-19.3, -5.43) * mm, "end": v(-19.3, -5.36) * mm});
            skLineSegment(sketch, "E441", {"start": v(-19.3, -5.36) * mm, "end": v(-19.3, -5.27) * mm});
            skLineSegment(sketch, "E442", {"start": v(-19.3, -5.27) * mm, "end": v(-19.14, -5.04) * mm});
            skLineSegment(sketch, "E443", {"start": v(-19.14, -5.04) * mm, "end": v(-19.11, -5.03) * mm});
            skLineSegment(sketch, "E444", {"start": v(-19.11, -5.03) * mm, "end": v(-19.08, -5) * mm});
            skLineSegment(sketch, "E445", {"start": v(-19.08, -5) * mm, "end": v(-18.76, -5) * mm});
            skLineSegment(sketch, "E446", {"start": v(-18.76, -5) * mm, "end": v(-18.73, -5.03) * mm});
            skLineSegment(sketch, "E447", {"start": v(-18.73, -5.03) * mm, "end": v(-18.7, -5.04) * mm});
            skLineSegment(sketch, "E448", {"start": v(-18.7, -5.04) * mm, "end": v(-18.54, -5.28) * mm});
            skLineSegment(sketch, "E449", {"start": v(-18.54, -5.28) * mm, "end": v(-18.54, -5.36) * mm});
            skLineSegment(sketch, "E450", {"start": v(8.76, -5.17) * mm, "end": v(8.76, -5.25) * mm});
            skLineSegment(sketch, "E451", {"start": v(8.76, -5.25) * mm, "end": v(8.6, -5.48) * mm});
            skLineSegment(sketch, "E452", {"start": v(8.6, -5.48) * mm, "end": v(8.57, -5.5) * mm});
            skLineSegment(sketch, "E453", {"start": v(8.57, -5.5) * mm, "end": v(8.54, -5.51) * mm});
            skLineSegment(sketch, "E454", {"start": v(8.54, -5.51) * mm, "end": v(8.22, -5.51) * mm});
            skLineSegment(sketch, "E455", {"start": v(8.22, -5.51) * mm, "end": v(8.2, -5.5) * mm});
            skLineSegment(sketch, "E456", {"start": v(8.2, -5.5) * mm, "end": v(8.16, -5.48) * mm});
            skLineSegment(sketch, "E457", {"start": v(8.16, -5.48) * mm, "end": v(8, -5.24) * mm});
            skLineSegment(sketch, "E458", {"start": v(8, -5.24) * mm, "end": v(8, -5.17) * mm});
            skLineSegment(sketch, "E459", {"start": v(8, -5.17) * mm, "end": v(8, -5.08) * mm});
            skLineSegment(sketch, "E460", {"start": v(8, -5.08) * mm, "end": v(8.16, -4.85) * mm});
            skLineSegment(sketch, "E461", {"start": v(8.16, -4.85) * mm, "end": v(8.2, -4.83) * mm});
            skLineSegment(sketch, "E462", {"start": v(8.2, -4.83) * mm, "end": v(8.22, -4.82) * mm});
            skLineSegment(sketch, "E463", {"start": v(8.22, -4.82) * mm, "end": v(8.54, -4.82) * mm});
            skLineSegment(sketch, "E464", {"start": v(8.54, -4.82) * mm, "end": v(8.57, -4.83) * mm});
            skLineSegment(sketch, "E465", {"start": v(8.57, -4.83) * mm, "end": v(8.6, -4.85) * mm});
            skLineSegment(sketch, "E466", {"start": v(8.6, -4.85) * mm, "end": v(8.76, -5.09) * mm});
            skLineSegment(sketch, "E467", {"start": v(8.76, -5.09) * mm, "end": v(8.76, -5.17) * mm});
            skLineSegment(sketch, "E468", {"start": v(4.37, 0.2) * mm, "end": v(4.37, 0.11) * mm});
            skLineSegment(sketch, "E469", {"start": v(4.37, 0.11) * mm, "end": v(4.2, -0.12) * mm});
            skLineSegment(sketch, "E470", {"start": v(4.2, -0.12) * mm, "end": v(4.18, -0.14) * mm});
            skLineSegment(sketch, "E471", {"start": v(4.18, -0.14) * mm, "end": v(4.15, -0.15) * mm});
            skLineSegment(sketch, "E472", {"start": v(4.15, -0.15) * mm, "end": v(3.83, -0.15) * mm});
            skLineSegment(sketch, "E473", {"start": v(3.83, -0.15) * mm, "end": v(3.8, -0.14) * mm});
            skLineSegment(sketch, "E474", {"start": v(3.8, -0.14) * mm, "end": v(3.77, -0.12) * mm});
            skLineSegment(sketch, "E475", {"start": v(3.77, -0.12) * mm, "end": v(3.6, 0.12) * mm});
            skLineSegment(sketch, "E476", {"start": v(3.6, 0.12) * mm, "end": v(3.6, 0.2) * mm});
            skLineSegment(sketch, "E477", {"start": v(3.6, 0.2) * mm, "end": v(3.6, 0.26) * mm});
            skLineSegment(sketch, "E478", {"start": v(3.6, 0.26) * mm, "end": v(3.72, 0.46) * mm});
            skLineSegment(sketch, "E479", {"start": v(3.72, 0.46) * mm, "end": v(3.92, 0.58) * mm});
            skLineSegment(sketch, "E480", {"start": v(3.92, 0.58) * mm, "end": v(3.99, 0.58) * mm});
            skLineSegment(sketch, "E481", {"start": v(3.99, 0.58) * mm, "end": v(4.05, 0.58) * mm});
            skLineSegment(sketch, "E482", {"start": v(4.05, 0.58) * mm, "end": v(4.26, 0.46) * mm});
            skLineSegment(sketch, "E483", {"start": v(4.26, 0.46) * mm, "end": v(4.37, 0.26) * mm});
            skLineSegment(sketch, "E484", {"start": v(4.37, 0.26) * mm, "end": v(4.37, 0.2) * mm});
            skLineSegment(sketch, "E485", {"start": v(2.29, 2.14) * mm, "end": v(2.29, 2.06) * mm});
            skLineSegment(sketch, "E486", {"start": v(2.29, 2.06) * mm, "end": v(2.12, 1.83) * mm});
            skLineSegment(sketch, "E487", {"start": v(2.12, 1.83) * mm, "end": v(2.1, 1.8) * mm});
            skLineSegment(sketch, "E488", {"start": v(2.1, 1.8) * mm, "end": v(2.07, 1.8) * mm});
            skLineSegment(sketch, "E489", {"start": v(2.07, 1.8) * mm, "end": v(1.74, 1.8) * mm});
            skLineSegment(sketch, "E490", {"start": v(1.74, 1.8) * mm, "end": v(1.72, 1.8) * mm});
            skLineSegment(sketch, "E491", {"start": v(1.72, 1.8) * mm, "end": v(1.69, 1.83) * mm});
            skLineSegment(sketch, "E492", {"start": v(1.69, 1.83) * mm, "end": v(1.52, 2.06) * mm});
            skLineSegment(sketch, "E493", {"start": v(1.52, 2.06) * mm, "end": v(1.52, 2.14) * mm});
            skLineSegment(sketch, "E494", {"start": v(1.52, 2.14) * mm, "end": v(1.52, 2.22) * mm});
            skLineSegment(sketch, "E495", {"start": v(1.52, 2.22) * mm, "end": v(1.69, 2.45) * mm});
            skLineSegment(sketch, "E496", {"start": v(1.69, 2.45) * mm, "end": v(1.72, 2.47) * mm});
            skLineSegment(sketch, "E497", {"start": v(1.72, 2.47) * mm, "end": v(1.74, 2.49) * mm});
            skLineSegment(sketch, "E498", {"start": v(1.74, 2.49) * mm, "end": v(2.07, 2.49) * mm});
            skLineSegment(sketch, "E499", {"start": v(2.07, 2.49) * mm, "end": v(2.1, 2.47) * mm});
            skLineSegment(sketch, "E500", {"start": v(2.1, 2.47) * mm, "end": v(2.12, 2.45) * mm});
            skLineSegment(sketch, "E501", {"start": v(2.12, 2.45) * mm, "end": v(2.29, 2.22) * mm});
            skLineSegment(sketch, "E502", {"start": v(2.29, 2.22) * mm, "end": v(2.29, 2.14) * mm});
            skLineSegment(sketch, "E503", {"start": v(6.29, 3.98) * mm, "end": v(6.29, 3.9) * mm});
            skLineSegment(sketch, "E504", {"start": v(6.29, 3.9) * mm, "end": v(6.13, 3.67) * mm});
            skLineSegment(sketch, "E505", {"start": v(6.13, 3.67) * mm, "end": v(6.1, 3.65) * mm});
            skLineSegment(sketch, "E506", {"start": v(6.1, 3.65) * mm, "end": v(6.07, 3.63) * mm});
            skLineSegment(sketch, "E507", {"start": v(6.07, 3.63) * mm, "end": v(5.74, 3.63) * mm});
            skLineSegment(sketch, "E508", {"start": v(5.74, 3.63) * mm, "end": v(5.72, 3.65) * mm});
            skLineSegment(sketch, "E509", {"start": v(5.72, 3.65) * mm, "end": v(5.69, 3.67) * mm});
            skLineSegment(sketch, "E510", {"start": v(5.69, 3.67) * mm, "end": v(5.52, 3.9) * mm});
            skLineSegment(sketch, "E511", {"start": v(5.52, 3.9) * mm, "end": v(5.52, 3.98) * mm});
            skLineSegment(sketch, "E512", {"start": v(5.52, 3.98) * mm, "end": v(5.52, 4.06) * mm});
            skLineSegment(sketch, "E513", {"start": v(5.52, 4.06) * mm, "end": v(5.69, 4.3) * mm});
            skLineSegment(sketch, "E514", {"start": v(5.69, 4.3) * mm, "end": v(5.72, 4.3) * mm});
            skLineSegment(sketch, "E515", {"start": v(5.72, 4.3) * mm, "end": v(5.74, 4.33) * mm});
            skLineSegment(sketch, "E516", {"start": v(5.74, 4.33) * mm, "end": v(6.07, 4.33) * mm});
            skLineSegment(sketch, "E517", {"start": v(6.07, 4.33) * mm, "end": v(6.1, 4.3) * mm});
            skLineSegment(sketch, "E518", {"start": v(6.1, 4.3) * mm, "end": v(6.13, 4.3) * mm});
            skLineSegment(sketch, "E519", {"start": v(6.13, 4.3) * mm, "end": v(6.29, 4.06) * mm});
            skLineSegment(sketch, "E520", {"start": v(6.29, 4.06) * mm, "end": v(6.29, 3.98) * mm});
            skLineSegment(sketch, "E521", {"start": v(16.13, -4.91) * mm, "end": v(16.13, -5) * mm});
            skLineSegment(sketch, "E522", {"start": v(16.13, -5) * mm, "end": v(15.97, -5.22) * mm});
            skLineSegment(sketch, "E523", {"start": v(15.97, -5.22) * mm, "end": v(15.94, -5.24) * mm});
            skLineSegment(sketch, "E524", {"start": v(15.94, -5.24) * mm, "end": v(15.9, -5.26) * mm});
            skLineSegment(sketch, "E525", {"start": v(15.9, -5.26) * mm, "end": v(15.59, -5.26) * mm});
            skLineSegment(sketch, "E526", {"start": v(15.59, -5.26) * mm, "end": v(15.56, -5.24) * mm});
            skLineSegment(sketch, "E527", {"start": v(15.56, -5.24) * mm, "end": v(15.53, -5.22) * mm});
            skLineSegment(sketch, "E528", {"start": v(15.53, -5.22) * mm, "end": v(15.37, -4.99) * mm});
            skLineSegment(sketch, "E529", {"start": v(15.37, -4.99) * mm, "end": v(15.37, -4.91) * mm});
            skLineSegment(sketch, "E530", {"start": v(15.37, -4.91) * mm, "end": v(15.37, -4.83) * mm});
            skLineSegment(sketch, "E531", {"start": v(15.37, -4.83) * mm, "end": v(15.53, -4.6) * mm});
            skLineSegment(sketch, "E532", {"start": v(15.53, -4.6) * mm, "end": v(15.56, -4.58) * mm});
            skLineSegment(sketch, "E533", {"start": v(15.56, -4.58) * mm, "end": v(15.59, -4.56) * mm});
            skLineSegment(sketch, "E534", {"start": v(15.59, -4.56) * mm, "end": v(15.9, -4.56) * mm});
            skLineSegment(sketch, "E535", {"start": v(15.9, -4.56) * mm, "end": v(15.94, -4.58) * mm});
            skLineSegment(sketch, "E536", {"start": v(15.94, -4.58) * mm, "end": v(15.97, -4.6) * mm});
            skLineSegment(sketch, "E537", {"start": v(15.97, -4.6) * mm, "end": v(16.13, -4.83) * mm});
            skLineSegment(sketch, "E538", {"start": v(16.13, -4.83) * mm, "end": v(16.13, -4.91) * mm});
            skLineSegment(sketch, "E539", {"start": v(11.94, 5) * mm, "end": v(11.94, 4.91) * mm});
            skLineSegment(sketch, "E540", {"start": v(11.94, 4.91) * mm, "end": v(11.78, 4.68) * mm});
            skLineSegment(sketch, "E541", {"start": v(11.78, 4.68) * mm, "end": v(11.75, 4.66) * mm});
            skLineSegment(sketch, "E542", {"start": v(11.75, 4.66) * mm, "end": v(11.72, 4.65) * mm});
            skLineSegment(sketch, "E543", {"start": v(11.72, 4.65) * mm, "end": v(11.4, 4.65) * mm});
            skLineSegment(sketch, "E544", {"start": v(11.4, 4.65) * mm, "end": v(11.37, 4.66) * mm});
            skLineSegment(sketch, "E545", {"start": v(11.37, 4.66) * mm, "end": v(11.34, 4.68) * mm});
            skLineSegment(sketch, "E546", {"start": v(11.34, 4.68) * mm, "end": v(11.18, 4.92) * mm});
            skLineSegment(sketch, "E547", {"start": v(11.18, 4.92) * mm, "end": v(11.18, 5) * mm});
            skLineSegment(sketch, "E548", {"start": v(11.18, 5) * mm, "end": v(11.18, 5.08) * mm});
            skLineSegment(sketch, "E549", {"start": v(11.18, 5.08) * mm, "end": v(11.34, 5.3) * mm});
            skLineSegment(sketch, "E550", {"start": v(11.34, 5.3) * mm, "end": v(11.37, 5.32) * mm});
            skLineSegment(sketch, "E551", {"start": v(11.37, 5.32) * mm, "end": v(11.4, 5.34) * mm});
            skLineSegment(sketch, "E552", {"start": v(11.4, 5.34) * mm, "end": v(11.72, 5.34) * mm});
            skLineSegment(sketch, "E553", {"start": v(11.72, 5.34) * mm, "end": v(11.75, 5.32) * mm});
            skLineSegment(sketch, "E554", {"start": v(11.75, 5.32) * mm, "end": v(11.78, 5.3) * mm});
            skLineSegment(sketch, "E555", {"start": v(11.78, 5.3) * mm, "end": v(11.94, 5.07) * mm});
            skLineSegment(sketch, "E556", {"start": v(11.94, 5.07) * mm, "end": v(11.94, 5) * mm});
            skLineSegment(sketch, "E557", {"start": v(4.5, 5.5) * mm, "end": v(4.5, 5.42) * mm});
            skLineSegment(sketch, "E558", {"start": v(4.5, 5.42) * mm, "end": v(4.35, 5.2) * mm});
            skLineSegment(sketch, "E559", {"start": v(4.35, 5.2) * mm, "end": v(4.32, 5.17) * mm});
            skLineSegment(sketch, "E560", {"start": v(4.32, 5.17) * mm, "end": v(4.29, 5.16) * mm});
            skLineSegment(sketch, "E561", {"start": v(4.29, 5.16) * mm, "end": v(3.97, 5.16) * mm});
            skLineSegment(sketch, "E562", {"start": v(3.97, 5.16) * mm, "end": v(3.94, 5.17) * mm});
            skLineSegment(sketch, "E563", {"start": v(3.94, 5.17) * mm, "end": v(3.9, 5.2) * mm});
            skLineSegment(sketch, "E564", {"start": v(3.9, 5.2) * mm, "end": v(3.75, 5.43) * mm});
            skLineSegment(sketch, "E565", {"start": v(3.75, 5.43) * mm, "end": v(3.75, 5.5) * mm});
            skLineSegment(sketch, "E566", {"start": v(3.75, 5.5) * mm, "end": v(3.75, 5.59) * mm});
            skLineSegment(sketch, "E567", {"start": v(3.75, 5.59) * mm, "end": v(3.9, 5.82) * mm});
            skLineSegment(sketch, "E568", {"start": v(3.9, 5.82) * mm, "end": v(3.94, 5.83) * mm});
            skLineSegment(sketch, "E569", {"start": v(3.94, 5.83) * mm, "end": v(3.97, 5.85) * mm});
            skLineSegment(sketch, "E570", {"start": v(3.97, 5.85) * mm, "end": v(4.29, 5.85) * mm});
            skLineSegment(sketch, "E571", {"start": v(4.29, 5.85) * mm, "end": v(4.32, 5.83) * mm});
            skLineSegment(sketch, "E572", {"start": v(4.32, 5.83) * mm, "end": v(4.35, 5.82) * mm});
            skLineSegment(sketch, "E573", {"start": v(4.35, 5.82) * mm, "end": v(4.5, 5.58) * mm});
            skLineSegment(sketch, "E574", {"start": v(4.5, 5.58) * mm, "end": v(4.5, 5.5) * mm});
            skLineSegment(sketch, "E575", {"start": v(0.45, 0.04) * mm, "end": v(0.45, -0.04) * mm});
            skLineSegment(sketch, "E576", {"start": v(0.45, -0.04) * mm, "end": v(0.28, -0.27) * mm});
            skLineSegment(sketch, "E577", {"start": v(0.28, -0.27) * mm, "end": v(0.25, -0.29) * mm});
            skLineSegment(sketch, "E578", {"start": v(0.25, -0.29) * mm, "end": v(0.22, -0.3) * mm});
            skLineSegment(sketch, "E579", {"start": v(0.22, -0.3) * mm, "end": v(-0.1, -0.3) * mm});
            skLineSegment(sketch, "E580", {"start": v(-0.1, -0.3) * mm, "end": v(-0.13, -0.29) * mm});
            skLineSegment(sketch, "E581", {"start": v(-0.13, -0.29) * mm, "end": v(-0.16, -0.27) * mm});
            skLineSegment(sketch, "E582", {"start": v(-0.16, -0.27) * mm, "end": v(-0.32, -0.04) * mm});
            skLineSegment(sketch, "E583", {"start": v(-0.32, -0.04) * mm, "end": v(-0.32, 0.04) * mm});
            skLineSegment(sketch, "E584", {"start": v(-0.32, 0.04) * mm, "end": v(-0.32, 0.1) * mm});
            skLineSegment(sketch, "E585", {"start": v(-0.32, 0.1) * mm, "end": v(-0.2, 0.31) * mm});
            skLineSegment(sketch, "E586", {"start": v(-0.2, 0.31) * mm, "end": v(0, 0.42) * mm});
            skLineSegment(sketch, "E587", {"start": v(0, 0.42) * mm, "end": v(0.06, 0.42) * mm});
            skLineSegment(sketch, "E588", {"start": v(0.06, 0.42) * mm, "end": v(0.13, 0.42) * mm});
            skLineSegment(sketch, "E589", {"start": v(0.13, 0.42) * mm, "end": v(0.33, 0.31) * mm});
            skLineSegment(sketch, "E590", {"start": v(0.33, 0.31) * mm, "end": v(0.45, 0.1) * mm});
            skLineSegment(sketch, "E591", {"start": v(0.45, 0.1) * mm, "end": v(0.45, 0.04) * mm});
            skLineSegment(sketch, "E592", {"start": v(-17.02, -1.6) * mm, "end": v(-17.02, -1.7) * mm});
            skLineSegment(sketch, "E593", {"start": v(-17.02, -1.7) * mm, "end": v(-17.18, -1.92) * mm});
            skLineSegment(sketch, "E594", {"start": v(-17.18, -1.92) * mm, "end": v(-17.2, -1.94) * mm});
            skLineSegment(sketch, "E595", {"start": v(-17.2, -1.94) * mm, "end": v(-17.24, -1.96) * mm});
            skLineSegment(sketch, "E596", {"start": v(-17.24, -1.96) * mm, "end": v(-17.56, -1.96) * mm});
            skLineSegment(sketch, "E597", {"start": v(-17.56, -1.96) * mm, "end": v(-17.59, -1.94) * mm});
            skLineSegment(sketch, "E598", {"start": v(-17.59, -1.94) * mm, "end": v(-17.62, -1.92) * mm});
            skLineSegment(sketch, "E599", {"start": v(-17.62, -1.92) * mm, "end": v(-17.78, -1.69) * mm});
            skLineSegment(sketch, "E600", {"start": v(-17.78, -1.69) * mm, "end": v(-17.78, -1.6) * mm});
            skLineSegment(sketch, "E601", {"start": v(-17.78, -1.6) * mm, "end": v(-17.78, -1.53) * mm});
            skLineSegment(sketch, "E602", {"start": v(-17.78, -1.53) * mm, "end": v(-17.62, -1.3) * mm});
            skLineSegment(sketch, "E603", {"start": v(-17.62, -1.3) * mm, "end": v(-17.59, -1.28) * mm});
            skLineSegment(sketch, "E604", {"start": v(-17.59, -1.28) * mm, "end": v(-17.56, -1.26) * mm});
            skLineSegment(sketch, "E605", {"start": v(-17.56, -1.26) * mm, "end": v(-17.24, -1.26) * mm});
            skLineSegment(sketch, "E606", {"start": v(-17.24, -1.26) * mm, "end": v(-17.2, -1.28) * mm});
            skLineSegment(sketch, "E607", {"start": v(-17.2, -1.28) * mm, "end": v(-17.18, -1.3) * mm});
            skLineSegment(sketch, "E608", {"start": v(-17.18, -1.3) * mm, "end": v(-17.02, -1.53) * mm});
            skLineSegment(sketch, "E609", {"start": v(-17.02, -1.53) * mm, "end": v(-17.02, -1.6) * mm});
            skLineSegment(sketch, "E610", {"start": v(-8.38, -3.13) * mm, "end": v(-8.38, -3.22) * mm});
            skLineSegment(sketch, "E611", {"start": v(-8.38, -3.22) * mm, "end": v(-8.54, -3.45) * mm});
            skLineSegment(sketch, "E612", {"start": v(-8.54, -3.45) * mm, "end": v(-8.57, -3.46) * mm});
            skLineSegment(sketch, "E613", {"start": v(-8.57, -3.46) * mm, "end": v(-8.6, -3.48) * mm});
            skLineSegment(sketch, "E614", {"start": v(-8.6, -3.48) * mm, "end": v(-8.92, -3.48) * mm});
            skLineSegment(sketch, "E615", {"start": v(-8.92, -3.48) * mm, "end": v(-8.95, -3.46) * mm});
            skLineSegment(sketch, "E616", {"start": v(-8.95, -3.46) * mm, "end": v(-8.98, -3.45) * mm});
            skLineSegment(sketch, "E617", {"start": v(-8.98, -3.45) * mm, "end": v(-9.14, -3.21) * mm});
            skLineSegment(sketch, "E618", {"start": v(-9.14, -3.21) * mm, "end": v(-9.14, -3.13) * mm});
            skLineSegment(sketch, "E619", {"start": v(-9.14, -3.13) * mm, "end": v(-9.14, -3.05) * mm});
            skLineSegment(sketch, "E620", {"start": v(-9.14, -3.05) * mm, "end": v(-8.98, -2.82) * mm});
            skLineSegment(sketch, "E621", {"start": v(-8.98, -2.82) * mm, "end": v(-8.95, -2.8) * mm});
            skLineSegment(sketch, "E622", {"start": v(-8.95, -2.8) * mm, "end": v(-8.92, -2.79) * mm});
            skLineSegment(sketch, "E623", {"start": v(-8.92, -2.79) * mm, "end": v(-8.6, -2.79) * mm});
            skLineSegment(sketch, "E624", {"start": v(-8.6, -2.79) * mm, "end": v(-8.57, -2.8) * mm});
            skLineSegment(sketch, "E625", {"start": v(-8.57, -2.8) * mm, "end": v(-8.54, -2.82) * mm});
            skLineSegment(sketch, "E626", {"start": v(-8.54, -2.82) * mm, "end": v(-8.38, -3.05) * mm});
            skLineSegment(sketch, "E627", {"start": v(-8.38, -3.05) * mm, "end": v(-8.38, -3.13) * mm});
            skLineSegment(sketch, "E628", {"start": v(-3.8, -0.66) * mm, "end": v(-3.8, -0.74) * mm});
            skLineSegment(sketch, "E629", {"start": v(-3.8, -0.74) * mm, "end": v(-3.97, -0.97) * mm});
            skLineSegment(sketch, "E630", {"start": v(-3.97, -0.97) * mm, "end": v(-4, -0.99) * mm});
            skLineSegment(sketch, "E631", {"start": v(-4, -0.99) * mm, "end": v(-4.03, -1) * mm});
            skLineSegment(sketch, "E632", {"start": v(-4.03, -1) * mm, "end": v(-4.35, -1) * mm});
            skLineSegment(sketch, "E633", {"start": v(-4.35, -1) * mm, "end": v(-4.38, -0.99) * mm});
            skLineSegment(sketch, "E634", {"start": v(-4.38, -0.99) * mm, "end": v(-4.41, -0.97) * mm});
            skLineSegment(sketch, "E635", {"start": v(-4.41, -0.97) * mm, "end": v(-4.57, -0.73) * mm});
            skLineSegment(sketch, "E636", {"start": v(-4.57, -0.73) * mm, "end": v(-4.57, -0.66) * mm});
            skLineSegment(sketch, "E637", {"start": v(-4.57, -0.66) * mm, "end": v(-4.57, -0.57) * mm});
            skLineSegment(sketch, "E638", {"start": v(-4.57, -0.57) * mm, "end": v(-4.41, -0.34) * mm});
            skLineSegment(sketch, "E639", {"start": v(-4.41, -0.34) * mm, "end": v(-4.38, -0.33) * mm});
            skLineSegment(sketch, "E640", {"start": v(-4.38, -0.33) * mm, "end": v(-4.35, -0.3) * mm});
            skLineSegment(sketch, "E641", {"start": v(-4.35, -0.3) * mm, "end": v(-4.03, -0.3) * mm});
            skLineSegment(sketch, "E642", {"start": v(-4.03, -0.3) * mm, "end": v(-4, -0.33) * mm});
            skLineSegment(sketch, "E643", {"start": v(-4, -0.33) * mm, "end": v(-3.97, -0.34) * mm});
            skLineSegment(sketch, "E644", {"start": v(-3.97, -0.34) * mm, "end": v(-3.8, -0.58) * mm});
            skLineSegment(sketch, "E645", {"start": v(-3.8, -0.58) * mm, "end": v(-3.8, -0.66) * mm});
            skLineSegment(sketch, "E646", {"start": v(-7.37, 1.18) * mm, "end": v(-7.37, 1.1) * mm});
            skLineSegment(sketch, "E647", {"start": v(-7.37, 1.1) * mm, "end": v(-7.53, 0.87) * mm});
            skLineSegment(sketch, "E648", {"start": v(-7.53, 0.87) * mm, "end": v(-7.56, 0.86) * mm});
            skLineSegment(sketch, "E649", {"start": v(-7.56, 0.86) * mm, "end": v(-7.59, 0.84) * mm});
            skLineSegment(sketch, "E650", {"start": v(-7.59, 0.84) * mm, "end": v(-7.9, 0.84) * mm});
            skLineSegment(sketch, "E651", {"start": v(-7.9, 0.84) * mm, "end": v(-7.94, 0.86) * mm});
            skLineSegment(sketch, "E652", {"start": v(-7.94, 0.86) * mm, "end": v(-7.97, 0.87) * mm});
            skLineSegment(sketch, "E653", {"start": v(-7.97, 0.87) * mm, "end": v(-8.13, 1.1) * mm});
            skLineSegment(sketch, "E654", {"start": v(-8.13, 1.1) * mm, "end": v(-8.13, 1.18) * mm});
            skLineSegment(sketch, "E655", {"start": v(-8.13, 1.18) * mm, "end": v(-8.13, 1.25) * mm});
            skLineSegment(sketch, "E656", {"start": v(-8.13, 1.25) * mm, "end": v(-8.02, 1.45) * mm});
            skLineSegment(sketch, "E657", {"start": v(-8.02, 1.45) * mm, "end": v(-7.81, 1.57) * mm});
            skLineSegment(sketch, "E658", {"start": v(-7.81, 1.57) * mm, "end": v(-7.75, 1.57) * mm});
            skLineSegment(sketch, "E659", {"start": v(-7.75, 1.57) * mm, "end": v(-7.68, 1.57) * mm});
            skLineSegment(sketch, "E660", {"start": v(-7.68, 1.57) * mm, "end": v(-7.48, 1.45) * mm});
            skLineSegment(sketch, "E661", {"start": v(-7.48, 1.45) * mm, "end": v(-7.37, 1.25) * mm});
            skLineSegment(sketch, "E662", {"start": v(-7.37, 1.25) * mm, "end": v(-7.37, 1.18) * mm});
            skLineSegment(sketch, "E663", {"start": v(-2.6, 1.12) * mm, "end": v(-2.6, 1.04) * mm});
            skLineSegment(sketch, "E664", {"start": v(-2.6, 1.04) * mm, "end": v(-2.76, 0.8) * mm});
            skLineSegment(sketch, "E665", {"start": v(-2.76, 0.8) * mm, "end": v(-2.8, 0.8) * mm});
            skLineSegment(sketch, "E666", {"start": v(-2.8, 0.8) * mm, "end": v(-2.82, 0.78) * mm});
            skLineSegment(sketch, "E667", {"start": v(-2.82, 0.78) * mm, "end": v(-3.15, 0.78) * mm});
            skLineSegment(sketch, "E668", {"start": v(-3.15, 0.78) * mm, "end": v(-3.18, 0.8) * mm});
            skLineSegment(sketch, "E669", {"start": v(-3.18, 0.8) * mm, "end": v(-3.2, 0.8) * mm});
            skLineSegment(sketch, "E670", {"start": v(-3.2, 0.8) * mm, "end": v(-3.37, 1.04) * mm});
            skLineSegment(sketch, "E671", {"start": v(-3.37, 1.04) * mm, "end": v(-3.37, 1.12) * mm});
            skLineSegment(sketch, "E672", {"start": v(-3.37, 1.12) * mm, "end": v(-3.37, 1.19) * mm});
            skLineSegment(sketch, "E673", {"start": v(-3.37, 1.19) * mm, "end": v(-3.25, 1.4) * mm});
            skLineSegment(sketch, "E674", {"start": v(-3.25, 1.4) * mm, "end": v(-3.05, 1.5) * mm});
            skLineSegment(sketch, "E675", {"start": v(-3.05, 1.5) * mm, "end": v(-2.98, 1.5) * mm});
            skLineSegment(sketch, "E676", {"start": v(-2.98, 1.5) * mm, "end": v(-2.92, 1.5) * mm});
            skLineSegment(sketch, "E677", {"start": v(-2.92, 1.5) * mm, "end": v(-2.71, 1.4) * mm});
            skLineSegment(sketch, "E678", {"start": v(-2.71, 1.4) * mm, "end": v(-2.6, 1.19) * mm});
            skLineSegment(sketch, "E679", {"start": v(-2.6, 1.19) * mm, "end": v(-2.6, 1.12) * mm});
            skLineSegment(sketch, "E680", {"start": v(16.64, 4.87) * mm, "end": v(16.64, 4.79) * mm});
            skLineSegment(sketch, "E681", {"start": v(16.64, 4.79) * mm, "end": v(16.48, 4.56) * mm});
            skLineSegment(sketch, "E682", {"start": v(16.48, 4.56) * mm, "end": v(16.45, 4.54) * mm});
            skLineSegment(sketch, "E683", {"start": v(16.45, 4.54) * mm, "end": v(16.42, 4.52) * mm});
            skLineSegment(sketch, "E684", {"start": v(16.42, 4.52) * mm, "end": v(16.1, 4.52) * mm});
            skLineSegment(sketch, "E685", {"start": v(16.1, 4.52) * mm, "end": v(16.07, 4.54) * mm});
            skLineSegment(sketch, "E686", {"start": v(16.07, 4.54) * mm, "end": v(16.04, 4.56) * mm});
            skLineSegment(sketch, "E687", {"start": v(16.04, 4.56) * mm, "end": v(15.88, 4.8) * mm});
            skLineSegment(sketch, "E688", {"start": v(15.88, 4.8) * mm, "end": v(15.88, 4.87) * mm});
            skLineSegment(sketch, "E689", {"start": v(15.88, 4.87) * mm, "end": v(15.88, 4.94) * mm});
            skLineSegment(sketch, "E690", {"start": v(15.88, 4.94) * mm, "end": v(15.99, 5.14) * mm});
            skLineSegment(sketch, "E691", {"start": v(15.99, 5.14) * mm, "end": v(16.19, 5.25) * mm});
            skLineSegment(sketch, "E692", {"start": v(16.19, 5.25) * mm, "end": v(16.26, 5.25) * mm});
            skLineSegment(sketch, "E693", {"start": v(16.26, 5.25) * mm, "end": v(16.32, 5.25) * mm});
            skLineSegment(sketch, "E694", {"start": v(16.32, 5.25) * mm, "end": v(16.53, 5.14) * mm});
            skLineSegment(sketch, "E695", {"start": v(16.53, 5.14) * mm, "end": v(16.64, 4.94) * mm});
            skLineSegment(sketch, "E696", {"start": v(16.64, 4.94) * mm, "end": v(16.64, 4.87) * mm});
            skLineSegment(sketch, "E697", {"start": v(-5.14, 4.42) * mm, "end": v(-5.14, 4.34) * mm});
            skLineSegment(sketch, "E698", {"start": v(-5.14, 4.34) * mm, "end": v(-5.3, 4.11) * mm});
            skLineSegment(sketch, "E699", {"start": v(-5.3, 4.11) * mm, "end": v(-5.33, 4.1) * mm});
            skLineSegment(sketch, "E700", {"start": v(-5.33, 4.1) * mm, "end": v(-5.36, 4.08) * mm});
            skLineSegment(sketch, "E701", {"start": v(-5.36, 4.08) * mm, "end": v(-5.69, 4.08) * mm});
            skLineSegment(sketch, "E702", {"start": v(-5.69, 4.08) * mm, "end": v(-5.71, 4.1) * mm});
            skLineSegment(sketch, "E703", {"start": v(-5.71, 4.1) * mm, "end": v(-5.75, 4.11) * mm});
            skLineSegment(sketch, "E704", {"start": v(-5.75, 4.11) * mm, "end": v(-5.9, 4.35) * mm});
            skLineSegment(sketch, "E705", {"start": v(-5.9, 4.35) * mm, "end": v(-5.9, 4.42) * mm});
            skLineSegment(sketch, "E706", {"start": v(-5.9, 4.42) * mm, "end": v(-5.9, 4.5) * mm});
            skLineSegment(sketch, "E707", {"start": v(-5.9, 4.5) * mm, "end": v(-5.75, 4.74) * mm});
            skLineSegment(sketch, "E708", {"start": v(-5.75, 4.74) * mm, "end": v(-5.71, 4.75) * mm});
            skLineSegment(sketch, "E709", {"start": v(-5.71, 4.75) * mm, "end": v(-5.69, 4.77) * mm});
            skLineSegment(sketch, "E710", {"start": v(-5.69, 4.77) * mm, "end": v(-5.36, 4.77) * mm});
            skLineSegment(sketch, "E711", {"start": v(-5.36, 4.77) * mm, "end": v(-5.33, 4.75) * mm});
            skLineSegment(sketch, "E712", {"start": v(-5.33, 4.75) * mm, "end": v(-5.3, 4.74) * mm});
            skLineSegment(sketch, "E713", {"start": v(-5.3, 4.74) * mm, "end": v(-5.14, 4.5) * mm});
            skLineSegment(sketch, "E714", {"start": v(-5.14, 4.5) * mm, "end": v(-5.14, 4.42) * mm});
            skLineSegment(sketch, "E715", {"start": v(-8.7, 3.92) * mm, "end": v(-8.7, 3.83) * mm});
            skLineSegment(sketch, "E716", {"start": v(-8.7, 3.83) * mm, "end": v(-8.86, 3.6) * mm});
            skLineSegment(sketch, "E717", {"start": v(-8.86, 3.6) * mm, "end": v(-8.89, 3.58) * mm});
            skLineSegment(sketch, "E718", {"start": v(-8.89, 3.58) * mm, "end": v(-8.92, 3.57) * mm});
            skLineSegment(sketch, "E719", {"start": v(-8.92, 3.57) * mm, "end": v(-9.24, 3.57) * mm});
            skLineSegment(sketch, "E720", {"start": v(-9.24, 3.57) * mm, "end": v(-9.27, 3.58) * mm});
            skLineSegment(sketch, "E721", {"start": v(-9.27, 3.58) * mm, "end": v(-9.3, 3.6) * mm});
            skLineSegment(sketch, "E722", {"start": v(-9.3, 3.6) * mm, "end": v(-9.46, 3.84) * mm});
            skLineSegment(sketch, "E723", {"start": v(-9.46, 3.84) * mm, "end": v(-9.46, 3.92) * mm});
            skLineSegment(sketch, "E724", {"start": v(-9.46, 3.92) * mm, "end": v(-9.46, 3.98) * mm});
            skLineSegment(sketch, "E725", {"start": v(-9.46, 3.98) * mm, "end": v(-9.35, 4.18) * mm});
            skLineSegment(sketch, "E726", {"start": v(-9.35, 4.18) * mm, "end": v(-9.15, 4.3) * mm});
            skLineSegment(sketch, "E727", {"start": v(-9.15, 4.3) * mm, "end": v(-9.08, 4.3) * mm});
            skLineSegment(sketch, "E728", {"start": v(-9.08, 4.3) * mm, "end": v(-9.01, 4.3) * mm});
            skLineSegment(sketch, "E729", {"start": v(-9.01, 4.3) * mm, "end": v(-8.81, 4.18) * mm});
            skLineSegment(sketch, "E730", {"start": v(-8.81, 4.18) * mm, "end": v(-8.7, 3.98) * mm});
            skLineSegment(sketch, "E731", {"start": v(-8.7, 3.98) * mm, "end": v(-8.7, 3.92) * mm});
            skLineSegment(sketch, "E732", {"start": v(-18.67, 3.92) * mm, "end": v(-18.67, 3.83) * mm});
            skLineSegment(sketch, "E733", {"start": v(-18.67, 3.83) * mm, "end": v(-18.83, 3.6) * mm});
            skLineSegment(sketch, "E734", {"start": v(-18.83, 3.6) * mm, "end": v(-18.86, 3.58) * mm});
            skLineSegment(sketch, "E735", {"start": v(-18.86, 3.58) * mm, "end": v(-18.89, 3.57) * mm});
            skLineSegment(sketch, "E736", {"start": v(-18.89, 3.57) * mm, "end": v(-19.21, 3.57) * mm});
            skLineSegment(sketch, "E737", {"start": v(-19.21, 3.57) * mm, "end": v(-19.24, 3.58) * mm});
            skLineSegment(sketch, "E738", {"start": v(-19.24, 3.58) * mm, "end": v(-19.27, 3.6) * mm});
            skLineSegment(sketch, "E739", {"start": v(-19.27, 3.6) * mm, "end": v(-19.43, 3.84) * mm});
            skLineSegment(sketch, "E740", {"start": v(-19.43, 3.84) * mm, "end": v(-19.43, 3.92) * mm});
            skLineSegment(sketch, "E741", {"start": v(-19.43, 3.92) * mm, "end": v(-19.43, 4) * mm});
            skLineSegment(sketch, "E742", {"start": v(-19.43, 4) * mm, "end": v(-19.27, 4.23) * mm});
            skLineSegment(sketch, "E743", {"start": v(-19.27, 4.23) * mm, "end": v(-19.24, 4.25) * mm});
            skLineSegment(sketch, "E744", {"start": v(-19.24, 4.25) * mm, "end": v(-19.21, 4.26) * mm});
            skLineSegment(sketch, "E745", {"start": v(-19.21, 4.26) * mm, "end": v(-18.89, 4.26) * mm});
            skLineSegment(sketch, "E746", {"start": v(-18.89, 4.26) * mm, "end": v(-18.86, 4.25) * mm});
            skLineSegment(sketch, "E747", {"start": v(-18.86, 4.25) * mm, "end": v(-18.83, 4.23) * mm});
            skLineSegment(sketch, "E748", {"start": v(-18.83, 4.23) * mm, "end": v(-18.67, 4) * mm});
            skLineSegment(sketch, "E749", {"start": v(-18.67, 4) * mm, "end": v(-18.67, 3.92) * mm});
            skLineSegment(sketch, "E750", {"start": v(-18.54, 1.88) * mm, "end": v(-18.54, 1.8) * mm});
            skLineSegment(sketch, "E751", {"start": v(-18.54, 1.8) * mm, "end": v(-18.7, 1.57) * mm});
            skLineSegment(sketch, "E752", {"start": v(-18.7, 1.57) * mm, "end": v(-18.73, 1.55) * mm});
            skLineSegment(sketch, "E753", {"start": v(-18.73, 1.55) * mm, "end": v(-18.76, 1.54) * mm});
            skLineSegment(sketch, "E754", {"start": v(-18.76, 1.54) * mm, "end": v(-19.08, 1.54) * mm});
            skLineSegment(sketch, "E755", {"start": v(-19.08, 1.54) * mm, "end": v(-19.11, 1.55) * mm});
            skLineSegment(sketch, "E756", {"start": v(-19.11, 1.55) * mm, "end": v(-19.14, 1.57) * mm});
            skLineSegment(sketch, "E757", {"start": v(-19.14, 1.57) * mm, "end": v(-19.3, 1.8) * mm});
            skLineSegment(sketch, "E758", {"start": v(-19.3, 1.8) * mm, "end": v(-19.3, 1.88) * mm});
            skLineSegment(sketch, "E759", {"start": v(-19.3, 1.88) * mm, "end": v(-19.3, 1.97) * mm});
            skLineSegment(sketch, "E760", {"start": v(-19.3, 1.97) * mm, "end": v(-19.14, 2.2) * mm});
            skLineSegment(sketch, "E761", {"start": v(-19.14, 2.2) * mm, "end": v(-19.11, 2.21) * mm});
            skLineSegment(sketch, "E762", {"start": v(-19.11, 2.21) * mm, "end": v(-19.08, 2.23) * mm});
            skLineSegment(sketch, "E763", {"start": v(-19.08, 2.23) * mm, "end": v(-18.76, 2.23) * mm});
            skLineSegment(sketch, "E764", {"start": v(-18.76, 2.23) * mm, "end": v(-18.73, 2.21) * mm});
            skLineSegment(sketch, "E765", {"start": v(-18.73, 2.21) * mm, "end": v(-18.7, 2.2) * mm});
            skLineSegment(sketch, "E766", {"start": v(-18.7, 2.2) * mm, "end": v(-18.54, 1.96) * mm});
            skLineSegment(sketch, "E767", {"start": v(-18.54, 1.96) * mm, "end": v(-18.54, 1.88) * mm});
            skLineSegment(sketch, "E768", {"start": v(-18.8, 5.63) * mm, "end": v(-18.8, 5.55) * mm});
            skLineSegment(sketch, "E769", {"start": v(-18.8, 5.55) * mm, "end": v(-18.96, 5.32) * mm});
            skLineSegment(sketch, "E770", {"start": v(-18.96, 5.32) * mm, "end": v(-18.99, 5.3) * mm});
            skLineSegment(sketch, "E771", {"start": v(-18.99, 5.3) * mm, "end": v(-19.02, 5.28) * mm});
            skLineSegment(sketch, "E772", {"start": v(-19.02, 5.28) * mm, "end": v(-19.34, 5.28) * mm});
            skLineSegment(sketch, "E773", {"start": v(-19.34, 5.28) * mm, "end": v(-19.37, 5.3) * mm});
            skLineSegment(sketch, "E774", {"start": v(-19.37, 5.3) * mm, "end": v(-19.4, 5.32) * mm});
            skLineSegment(sketch, "E775", {"start": v(-19.4, 5.32) * mm, "end": v(-19.56, 5.55) * mm});
            skLineSegment(sketch, "E776", {"start": v(-19.56, 5.55) * mm, "end": v(-19.56, 5.63) * mm});
            skLineSegment(sketch, "E777", {"start": v(-19.56, 5.63) * mm, "end": v(-19.56, 5.7) * mm});
            skLineSegment(sketch, "E778", {"start": v(-19.56, 5.7) * mm, "end": v(-19.45, 5.9) * mm});
            skLineSegment(sketch, "E779", {"start": v(-19.45, 5.9) * mm, "end": v(-19.24, 6.01) * mm});
            skLineSegment(sketch, "E780", {"start": v(-19.24, 6.01) * mm, "end": v(-19.18, 6.01) * mm});
            skLineSegment(sketch, "E781", {"start": v(-19.18, 6.01) * mm, "end": v(-19.11, 6.01) * mm});
            skLineSegment(sketch, "E782", {"start": v(-19.11, 6.01) * mm, "end": v(-18.9, 5.9) * mm});
            skLineSegment(sketch, "E783", {"start": v(-18.9, 5.9) * mm, "end": v(-18.8, 5.7) * mm});
            skLineSegment(sketch, "E784", {"start": v(-18.8, 5.7) * mm, "end": v(-18.8, 5.63) * mm});
            skLineSegment(sketch, "E785", {"start": v(-22.23, -6.18) * mm, "end": v(22.23, -6.18) * mm});
            skLineSegment(sketch, "E786", {"start": v(22.23, 6.52) * mm, "end": v(22.23, -6.18) * mm});
            skLineSegment(sketch, "E787", {"start": v(22.23, 6.52) * mm, "end": v(-22.23, 6.52) * mm});
            skLineSegment(sketch, "E788", {"start": v(-22.23, -6.18) * mm, "end": v(-22.23, 6.52) * mm});
            skLineSegment(sketch, "E789", {"start": v(-19.11, 1.55) * mm, "end": v(-18.73, 2.21) * mm});
            skLineSegment(sketch, "E790", {"start": v(-19.3, 1.88) * mm, "end": v(-18.54, 1.88) * mm});
            skLineSegment(sketch, "E791", {"start": v(-19.11, 2.21) * mm, "end": v(-18.73, 1.55) * mm});
            skLineSegment(sketch, "E792", {"start": v(15.68, 4.87) * mm, "end": v(16.83, 4.87) * mm});
            skLineSegment(sketch, "E793", {"start": v(16.54, 5.36) * mm, "end": v(15.97, 4.37) * mm});
            skLineSegment(sketch, "E794", {"start": v(16.54, 4.37) * mm, "end": v(15.97, 5.36) * mm});
            skPoint(sketch, "E795", {"position": v(16.26, 4.87) * mm});
            skLineSegment(sketch, "E796", {"start": v(-19.5, 1.88) * mm, "end": v(-18.35, 1.88) * mm});
            skLineSegment(sketch, "E797", {"start": v(-19.2, 2.38) * mm, "end": v(-18.64, 1.39) * mm});
            skLineSegment(sketch, "E798", {"start": v(-19.2, 1.39) * mm, "end": v(-18.64, 2.38) * mm});
            skLineSegment(sketch, "E799", {"start": v(-19.5, -5.36) * mm, "end": v(-18.35, -5.36) * mm});
            skLineSegment(sketch, "E800", {"start": v(-18.64, -4.86) * mm, "end": v(-19.2, -5.85) * mm});
            skLineSegment(sketch, "E801", {"start": v(-19.59, -4.39) * mm, "end": v(-19.02, -3.4) * mm});
            skLineSegment(sketch, "E802", {"start": v(-19.88, -3.9) * mm, "end": v(-18.73, -3.9) * mm});
            skLineSegment(sketch, "E803", {"start": v(-17.68, -2.1) * mm, "end": v(-17.11, -1.11) * mm});
            skLineSegment(sketch, "E804", {"start": v(-17.97, -1.6) * mm, "end": v(-16.83, -1.6) * mm});
            skLineSegment(sketch, "E805", {"start": v(-9.33, -3.13) * mm, "end": v(-8.2, -3.13) * mm});
            skLineSegment(sketch, "E806", {"start": v(-8.48, -2.64) * mm, "end": v(-9.05, -3.63) * mm});
            skLineSegment(sketch, "E807", {"start": v(-6.49, -3.97) * mm, "end": v(-5.35, -3.97) * mm});
            skLineSegment(sketch, "E808", {"start": v(-6.2, -4.47) * mm, "end": v(-5.63, -3.48) * mm});
            skLineSegment(sketch, "E809", {"start": v(-7.46, 0.69) * mm, "end": v(-8.03, 1.68) * mm});
            skLineSegment(sketch, "E810", {"start": v(-8.03, 0.69) * mm, "end": v(-7.46, 1.68) * mm});
            skLineSegment(sketch, "E811", {"start": v(-8.8, 3.42) * mm, "end": v(-9.37, 4.41) * mm});
            skLineSegment(sketch, "E812", {"start": v(-9.37, 3.42) * mm, "end": v(-8.8, 4.41) * mm});
            skLineSegment(sketch, "E813", {"start": v(-4.48, -1.15) * mm, "end": v(-3.9, -0.16) * mm});
            skLineSegment(sketch, "E814", {"start": v(-4.48, -0.16) * mm, "end": v(-3.9, -1.15) * mm});
            skLineSegment(sketch, "E815", {"start": v(-6.1, 4.42) * mm, "end": v(-4.95, 4.42) * mm});
            skLineSegment(sketch, "E816", {"start": v(-5.24, 3.93) * mm, "end": v(-5.8, 4.92) * mm});
            skLineSegment(sketch, "E817", {"start": v(-3.27, 1.62) * mm, "end": v(-2.7, 0.63) * mm});
            skLineSegment(sketch, "E818", {"start": v(-3.27, 0.63) * mm, "end": v(-2.7, 1.62) * mm});
            skLineSegment(sketch, "E819", {"start": v(-0.22, -0.45) * mm, "end": v(0.35, 0.54) * mm});
            skLineSegment(sketch, "E820", {"start": v(-0.5, 0.04) * mm, "end": v(0.64, 0.04) * mm});
            skLineSegment(sketch, "E821", {"start": v(1.62, 1.64) * mm, "end": v(2.2, 2.63) * mm});
            skLineSegment(sketch, "E822", {"start": v(1.33, 2.14) * mm, "end": v(2.48, 2.14) * mm});
            skLineSegment(sketch, "E823", {"start": v(3.56, 5.5) * mm, "end": v(4.7, 5.5) * mm});
            skLineSegment(sketch, "E824", {"start": v(4.41, 5) * mm, "end": v(3.84, 6) * mm});
            skLineSegment(sketch, "E825", {"start": v(5.62, 3.48) * mm, "end": v(6.2, 4.47) * mm});
            skLineSegment(sketch, "E826", {"start": v(5.33, 3.98) * mm, "end": v(6.48, 3.98) * mm});
            skLineSegment(sketch, "E827", {"start": v(3.42, 0.2) * mm, "end": v(4.56, 0.2) * mm});
            skLineSegment(sketch, "E828", {"start": v(4.27, -0.3) * mm, "end": v(3.7, 0.69) * mm});
            skLineSegment(sketch, "E829", {"start": v(8.95, -5.17) * mm, "end": v(7.81, -5.17) * mm});
            skLineSegment(sketch, "E830", {"start": v(8.1, -4.67) * mm, "end": v(8.67, -5.66) * mm});
            skLineSegment(sketch, "E831", {"start": v(15.46, -4.42) * mm, "end": v(16.03, -5.4) * mm});
            skLineSegment(sketch, "E832", {"start": v(15.18, -4.91) * mm, "end": v(16.32, -4.91) * mm});
            skLineSegment(sketch, "E833", {"start": v(10.99, 5) * mm, "end": v(12.13, 5) * mm});
            skLineSegment(sketch, "E834", {"start": v(11.84, 4.5) * mm, "end": v(11.27, 5.49) * mm});
            skLineSegment(sketch, "E835", {"start": v(-19.62, 3.92) * mm, "end": v(-18.48, 3.92) * mm});
            skLineSegment(sketch, "E836", {"start": v(-18.76, 3.42) * mm, "end": v(-19.34, 4.41) * mm});
            skLineSegment(sketch, "E837", {"start": v(-18.9, 5.14) * mm, "end": v(-19.46, 6.12) * mm});
            skLineSegment(sketch, "E838", {"start": v(-19.75, 5.63) * mm, "end": v(-18.6, 5.63) * mm});
            skSolve(sketch);
        }
        {
            var Q0;
            Q0=makeQuery(id+"F0.imprint","IMPRINT",FACE,{"disambiguationData":[TD([[makeQuery(id+"F0.imprint","IMPRINT",EDGE,{"derivedFrom":sQuery(id+"F0.wireOp",EDGE,"E0")}),1.0]])]});
            var sketch = newSketch(context, id + "F1", { "sketchPlane" : qUnion([Q0])});
            skLineSegment(sketch, "E839.0", {"start": v(-22.23, -6.18) * mm, "end": v(-22.23, 6.52) * mm});
            skPoint(sketch, "E839.1", {"position": v(-22.23, 6.52) * mm});
            skLineSegment(sketch, "E839.2", {"start": v(22.23, 6.52) * mm, "end": v(-22.23, 6.52) * mm});
            skPoint(sketch, "E839.3", {"position": v(22.23, 6.52) * mm});
            skLineSegment(sketch, "E839.4", {"start": v(22.23, 6.52) * mm, "end": v(22.23, -6.18) * mm});
            skPoint(sketch, "E839.5", {"position": v(22.23, -6.18) * mm});
            skLineSegment(sketch, "E839.6", {"start": v(-22.23, -6.18) * mm, "end": v(22.23, -6.18) * mm});
            skPoint(sketch, "E839.7", {"position": v(-22.23, -6.18) * mm});
            skSolve(sketch);
        }
        {
            var Q0;
            Q0 = qSketchRegion(id + "F1", true);
            extrude(context, id + "F2", {"entities" : qUnion([Q0]), "depth" : 12.7 * mm, "offsetDistance" : 25.4 * mm});
        }
        {
            var Q0;
            Q0=makeQuery(id+"F2.opExtrude","CAP_FACE",FACE,{"disambiguationData":[OSD([sQuery(id+"F1.wireOp",EDGE,"E839.0"),sQuery(id+"F1.wireOp",EDGE,"E839.2"),sQuery(id+"F1.wireOp",EDGE,"E839.4"),sQuery(id+"F1.wireOp",EDGE,"E839.6")])],"isStart":false});
            var sketch = newSketch(context, id + "F3", { "sketchPlane" : qUnion([Q0])});
            skPoint(sketch, "E840.0", {"position": v(16.26, 4.87) * mm});
            skPoint(sketch, "E840.1", {"position": v(-18.92, -5.36) * mm});
            skPoint(sketch, "E840.2", {"position": v(-19.3, -3.9) * mm});
            skPoint(sketch, "E840.3", {"position": v(-17.4, -1.6) * mm});
            skPoint(sketch, "E840.4", {"position": v(-18.92, 1.88) * mm});
            skPoint(sketch, "E840.5", {"position": v(-19.05, 3.92) * mm});
            skPoint(sketch, "E840.6", {"position": v(-19.18, 5.63) * mm});
            skPoint(sketch, "E840.7", {"position": v(-9.08, 3.92) * mm});
            skPoint(sketch, "E840.8", {"position": v(-7.75, 1.18) * mm});
            skPoint(sketch, "E840.9", {"position": v(-8.76, -3.13) * mm});
            skPoint(sketch, "E840.10", {"position": v(-5.92, -3.97) * mm});
            skPoint(sketch, "E840.11", {"position": v(-4.2, -0.66) * mm});
            skPoint(sketch, "E840.12", {"position": v(-2.98, 1.12) * mm});
            skPoint(sketch, "E840.13", {"position": v(-5.52, 4.42) * mm});
            skPoint(sketch, "E840.14", {"position": v(0.06, 0.04) * mm});
            skPoint(sketch, "E840.15", {"position": v(8.38, -5.17) * mm});
            skPoint(sketch, "E840.16", {"position": v(3.99, 0.2) * mm});
            skPoint(sketch, "E840.17", {"position": v(1.9, 2.14) * mm});
            skPoint(sketch, "E840.18", {"position": v(4.13, 5.5) * mm});
            skPoint(sketch, "E840.19", {"position": v(5.9, 3.98) * mm});
            skPoint(sketch, "E840.20", {"position": v(11.56, 5) * mm});
            skPoint(sketch, "E840.21", {"position": v(15.75, -4.91) * mm});
            skCircle(sketch, "E841", {"center": v(-18.92, -5.36) * mm, "radius": 0.38 * mm});
            skCircle(sketch, "E842", {"center": v(-19.3, -3.9) * mm, "radius": 0.38 * mm});
            skCircle(sketch, "E843", {"center": v(-17.4, -1.6) * mm, "radius": 0.38 * mm});
            skCircle(sketch, "E844", {"center": v(-18.92, 1.88) * mm, "radius": 0.4 * mm});
            skCircle(sketch, "E845", {"center": v(-19.05, 3.92) * mm, "radius": 0.38 * mm});
            skCircle(sketch, "E846", {"center": v(-19.18, 5.63) * mm, "radius": 0.38 * mm});
            skCircle(sketch, "E847", {"center": v(-9.08, 3.92) * mm, "radius": 0.38 * mm});
            skCircle(sketch, "E848", {"center": v(-7.75, 1.18) * mm, "radius": 0.38 * mm});
            skCircle(sketch, "E849", {"center": v(-8.76, -3.13) * mm, "radius": 0.38 * mm});
            skCircle(sketch, "E850", {"center": v(-5.92, -3.97) * mm, "radius": 0.38 * mm});
            skCircle(sketch, "E851", {"center": v(-4.2, -0.66) * mm, "radius": 0.38 * mm});
            skCircle(sketch, "E852", {"center": v(-2.98, 1.12) * mm, "radius": 0.38 * mm});
            skCircle(sketch, "E853", {"center": v(-5.52, 4.42) * mm, "radius": 0.38 * mm});
            skCircle(sketch, "E854", {"center": v(0.06, 0.04) * mm, "radius": 0.38 * mm});
            skCircle(sketch, "E855", {"center": v(1.9, 2.14) * mm, "radius": 0.38 * mm});
            skCircle(sketch, "E856", {"center": v(3.99, 0.2) * mm, "radius": 0.38 * mm});
            skCircle(sketch, "E857", {"center": v(8.38, -5.17) * mm, "radius": 0.38 * mm});
            skCircle(sketch, "E858", {"center": v(5.9, 3.98) * mm, "radius": 0.38 * mm});
            skCircle(sketch, "E859", {"center": v(4.13, 5.5) * mm, "radius": 0.38 * mm});
            skCircle(sketch, "E860", {"center": v(11.56, 5) * mm, "radius": 0.38 * mm});
            skCircle(sketch, "E861", {"center": v(16.26, 4.87) * mm, "radius": 0.38 * mm});
            skCircle(sketch, "E862", {"center": v(15.75, -4.91) * mm, "radius": 0.38 * mm});
            skSolve(sketch);
        }
        {
            var Q0;
            Q0 = qSketchRegion(id + "F3", true);
            var Q1;
            Q1=makeQuery(id+"F2.opExtrude","CAP_FACE",FACE,{"disambiguationData":[OSD([sQuery(id+"F1.wireOp",EDGE,"E839.0"),sQuery(id+"F1.wireOp",EDGE,"E839.2"),sQuery(id+"F1.wireOp",EDGE,"E839.4"),sQuery(id+"F1.wireOp",EDGE,"E839.6")])],"isStart":true});
            extrude(context, id + "F4", {"entities" : qUnion([Q0]), "operationType" : NewBodyOperationType.REMOVE, "endBound" : BoundingType.THROUGH_ALL, "oppositeDirection" : true, "depth" : 25.4 * mm, "endBoundEntityFace" : qUnion([Q1]), "offsetDistance" : 25.4 * mm});
        }
        {
            var Q0;
            Q0=makeQuery(id+"F2.opExtrude","CAP_FACE",FACE,{"disambiguationData":[OSD([sQuery(id+"F1.wireOp",EDGE,"E839.0"),sQuery(id+"F1.wireOp",EDGE,"E839.2"),sQuery(id+"F1.wireOp",EDGE,"E839.4"),sQuery(id+"F1.wireOp",EDGE,"E839.6")])],"isStart":false});
            var sketch = newSketch(context, id + "F5", { "sketchPlane" : qUnion([Q0])});
            skLineSegment(sketch, "E863.bottom", {"start": v(0, 6.52) * mm, "end": v(-2.54, 6.52) * mm});
            skLineSegment(sketch, "E863.top", {"start": v(0, 9.06) * mm, "end": v(-2.54, 9.06) * mm});
            skLineSegment(sketch, "E863.left", {"start": v(0, 6.52) * mm, "end": v(0, 9.06) * mm});
            skLineSegment(sketch, "E863.right", {"start": v(-2.54, 6.52) * mm, "end": v(-2.54, 9.06) * mm});
            skSolve(sketch);
        }
        {
            var Q0;
            Q0 = qSketchRegion(id + "F5", true);
            var Q1;
            Q1=makeQuery(id+"F2.opExtrude","CAP_FACE",FACE,{"disambiguationData":[OSD([sQuery(id+"F1.wireOp",EDGE,"E839.0"),sQuery(id+"F1.wireOp",EDGE,"E839.2"),sQuery(id+"F1.wireOp",EDGE,"E839.4"),sQuery(id+"F1.wireOp",EDGE,"E839.6")])],"isStart":true});
            extrude(context, id + "F6", {"entities" : qUnion([Q0]), "operationType" : NewBodyOperationType.ADD, "endBound" : BoundingType.UP_TO_SURFACE, "oppositeDirection" : true, "depth" : 25.4 * mm, "endBoundEntityFace" : qUnion([Q1]), "offsetDistance" : 25.4 * mm});
        }
        {
            var Q0;
            Q0=makeQuery(id+"F6.boolean.opBoolean","MERGE",FACE,{"derivedFrom":[makeQuery(id+"F2.opExtrude","CAP_FACE",FACE,{"disambiguationData":[OSD([sQuery(id+"F1.wireOp",EDGE,"E839.0"),sQuery(id+"F1.wireOp",EDGE,"E839.2"),sQuery(id+"F1.wireOp",EDGE,"E839.4"),sQuery(id+"F1.wireOp",EDGE,"E839.6")])],"isStart":false}),makeQuery(id+"F6.opExtrude","CAP_FACE",FACE,{"disambiguationData":[OSD([sQuery(id+"F5.wireOp",EDGE,"E863.bottom"),sQuery(id+"F5.wireOp",EDGE,"E863.top"),sQuery(id+"F5.wireOp",EDGE,"E863.left"),sQuery(id+"F5.wireOp",EDGE,"E863.right")])],"isStart":true})]});
            var sketch = newSketch(context, id + "F7", { "sketchPlane" : qUnion([Q0])});
            skLineSegment(sketch, "E864.bottom", {"start": v(-4.1, 6.52) * mm, "end": v(2.26, 6.52) * mm});
            skLineSegment(sketch, "E864.top", {"start": v(-4.1, 5.25) * mm, "end": v(2.26, 5.25) * mm});
            skLineSegment(sketch, "E864.left", {"start": v(-4.1, 6.52) * mm, "end": v(-4.1, 5.25) * mm});
            skLineSegment(sketch, "E864.right", {"start": v(2.26, 6.52) * mm, "end": v(2.26, 5.25) * mm});
            skLineSegment(sketch, "E865.bottom", {"start": v(-4.17, -6.18) * mm, "end": v(2.18, -6.18) * mm});
            skLineSegment(sketch, "E865.top", {"start": v(-4.17, -2.37) * mm, "end": v(2.18, -2.37) * mm});
            skLineSegment(sketch, "E865.left", {"start": v(-4.17, -6.18) * mm, "end": v(-4.17, -2.37) * mm});
            skLineSegment(sketch, "E865.right", {"start": v(2.18, -6.18) * mm, "end": v(2.18, -2.37) * mm});
            skLineSegment(sketch, "E866.bottom", {"start": v(22.23, 3.21) * mm, "end": v(20.96, 3.21) * mm});
            skLineSegment(sketch, "E866.top", {"start": v(22.23, -3.14) * mm, "end": v(20.96, -3.14) * mm});
            skLineSegment(sketch, "E866.left", {"start": v(22.23, 3.21) * mm, "end": v(22.23, -3.14) * mm});
            skLineSegment(sketch, "E866.right", {"start": v(20.96, 3.21) * mm, "end": v(20.96, -3.14) * mm});
            skLineSegment(sketch, "E867.bottom", {"start": v(-22.23, 2.87) * mm, "end": v(-20.96, 2.87) * mm});
            skLineSegment(sketch, "E867.top", {"start": v(-22.23, -2.21) * mm, "end": v(-20.96, -2.21) * mm});
            skLineSegment(sketch, "E867.left", {"start": v(-22.23, 2.87) * mm, "end": v(-22.23, -2.21) * mm});
            skLineSegment(sketch, "E867.right", {"start": v(-20.96, 2.87) * mm, "end": v(-20.96, -2.21) * mm});
            skSolve(sketch);
        }
        {
            var Q0;
            Q0 = qSketchRegion(id + "F7", true);
            extrude(context, id + "F8", {"entities" : qUnion([Q0]), "operationType" : NewBodyOperationType.ADD, "depth" : 1.02 * mm, "offsetDistance" : 25.4 * mm});
        }
    });
